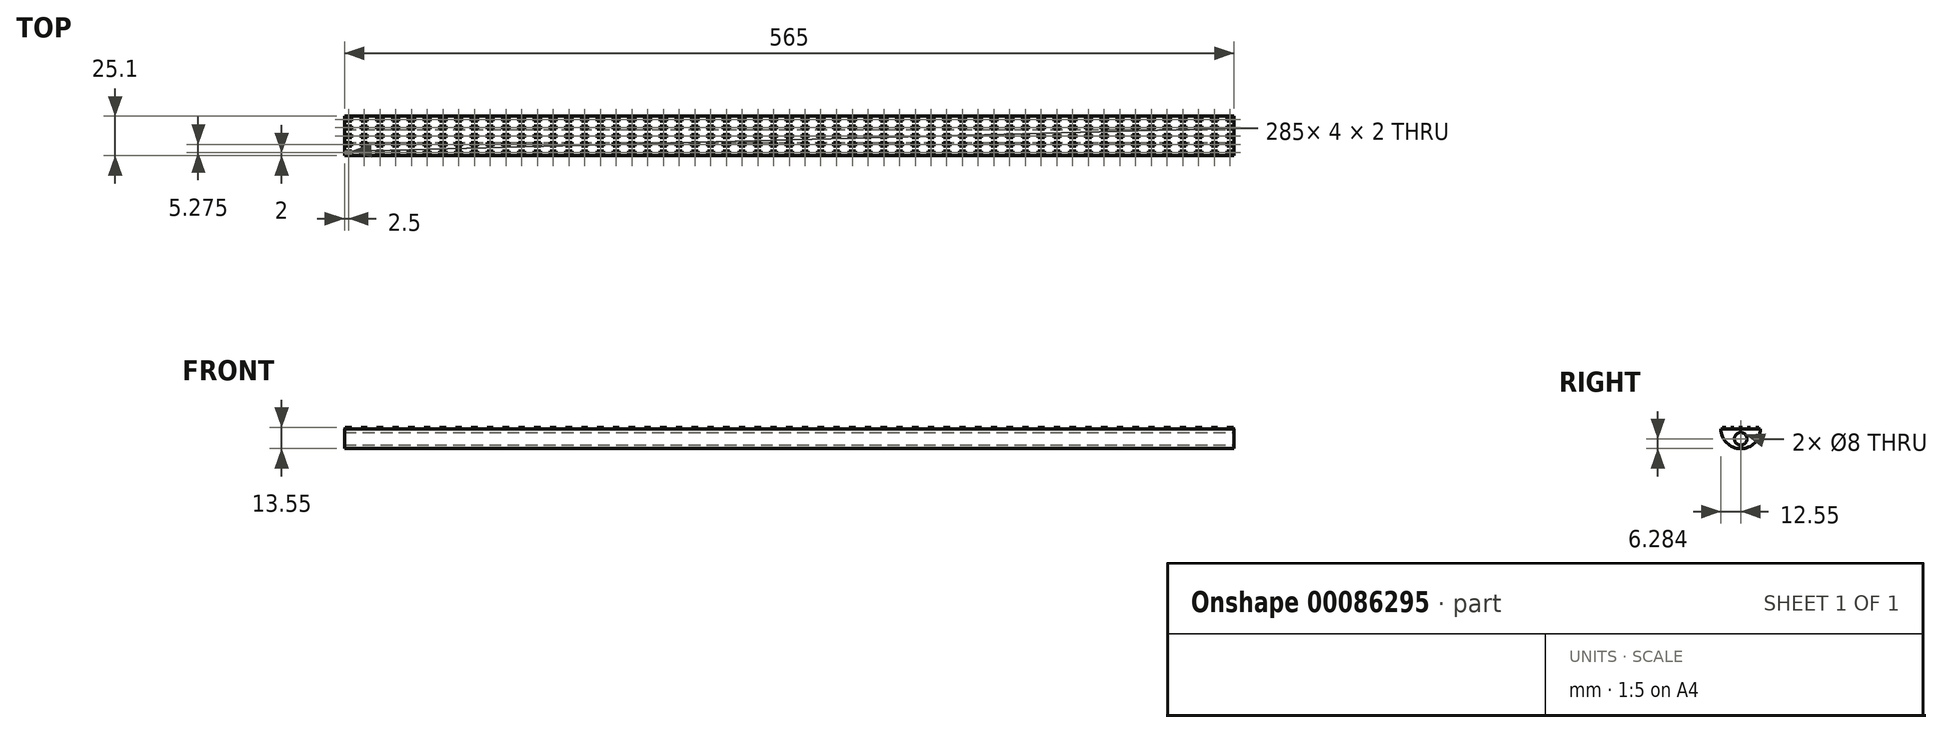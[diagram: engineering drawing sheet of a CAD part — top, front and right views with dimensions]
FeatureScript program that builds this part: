
annotation { "Feature Type Name" : "Feature", "Feature Type Description" : "" }
export const myFeature = defineFeature(function(context is Context, id is Id, definition is map)
    precondition{}
    {
        {
            var Q0;
            Q0=qCreatedBy(makeId("Right.planeOp"),FACE);
            var sketch = newSketch(context, id + "F0", { "sketchPlane" : qUnion([Q0])});
            skArc(sketch, "E0", {"start": v(-12.55, 0) * mm, "mid": v(0, -12.55) * mm, "end": v(12.55, 0) * mm});
            skLineSegment(sketch, "E1", {"start": v(-12.55, 0) * mm, "end": v(12.55, 0) * mm});
            skSolve(sketch);
        }
        {
            var Q0;
            Q0=qSketchRegion(id+"F0",true);
            extrude(context, id + "F1", {"entities" : qUnion([Q0]), "endBound" : BoundingType.SYMMETRIC, "depth" : 565 * mm});
        }
        {
            var Q0;
            Q0=makeQuery(id+"F1.opExtrude","SWEPT_FACE",FACE,{"disambiguationData":[OSD([sQuery(id+"F0.wireOp",EDGE,"E1")])]});
            var sketch = newSketch(context, id + "F2", { "sketchPlane" : qUnion([Q0])});
            skLineSegment(sketch, "E2.bottom", {"start": v(-282, 11.55) * mm, "end": v(-278, 11.55) * mm});
            skLineSegment(sketch, "E2.top", {"start": v(-282, 9.55) * mm, "end": v(-278, 9.55) * mm});
            skLineSegment(sketch, "E2.left", {"start": v(-282, 11.55) * mm, "end": v(-282, 9.55) * mm});
            skLineSegment(sketch, "E2.right", {"start": v(-278, 11.55) * mm, "end": v(-278, 9.55) * mm});
            skLineSegment(sketch, "E3.1.0.0", {"start": v(-282, 6.27) * mm, "end": v(-282, 4.27) * mm});
            skLineSegment(sketch, "E3.1.0.1", {"start": v(-282, 6.27) * mm, "end": v(-278, 6.27) * mm});
            skLineSegment(sketch, "E3.1.0.2", {"start": v(-278, 6.27) * mm, "end": v(-278, 4.27) * mm});
            skLineSegment(sketch, "E3.1.0.3", {"start": v(-282, 4.27) * mm, "end": v(-278, 4.27) * mm});
            skLineSegment(sketch, "E3.2.0.0", {"start": v(-282, 1) * mm, "end": v(-282, -1) * mm});
            skLineSegment(sketch, "E3.2.0.1", {"start": v(-282, 1) * mm, "end": v(-278, 1) * mm});
            skLineSegment(sketch, "E3.2.0.2", {"start": v(-278, 1) * mm, "end": v(-278, -1) * mm});
            skLineSegment(sketch, "E3.2.0.3", {"start": v(-282, -1) * mm, "end": v(-278, -1) * mm});
            skLineSegment(sketch, "E3.direction1", {"start": v(-278, 9.55) * mm, "end": v(-278, 4.27) * mm, "construction": true});
            skLineSegment(sketch, "E4.0.3.0", {"start": v(-282, -4.28) * mm, "end": v(-282, -6.28) * mm});
            skLineSegment(sketch, "E4.3.3.0", {"start": v(-282, -4.28) * mm, "end": v(-278, -4.28) * mm});
            skLineSegment(sketch, "E4.6.3.0", {"start": v(-278, -4.28) * mm, "end": v(-278, -6.28) * mm});
            skLineSegment(sketch, "E4.9.3.0", {"start": v(-282, -6.28) * mm, "end": v(-278, -6.28) * mm});
            skLineSegment(sketch, "E5.0.4.0", {"start": v(-282, -9.55) * mm, "end": v(-282, -11.55) * mm});
            skLineSegment(sketch, "E5.3.4.0", {"start": v(-282, -9.55) * mm, "end": v(-278, -9.55) * mm});
            skLineSegment(sketch, "E5.6.4.0", {"start": v(-278, -9.55) * mm, "end": v(-278, -11.55) * mm});
            skLineSegment(sketch, "E5.9.4.0", {"start": v(-282, -11.55) * mm, "end": v(-278, -11.55) * mm});
            skLineSegment(sketch, "E6.1.0.0", {"start": v(-272, -9.55) * mm, "end": v(-272, -11.55) * mm});
            skLineSegment(sketch, "E6.1.0.1", {"start": v(-268, -9.55) * mm, "end": v(-268, -11.55) * mm});
            skLineSegment(sketch, "E6.1.0.2", {"start": v(-272, -9.55) * mm, "end": v(-268, -9.55) * mm});
            skLineSegment(sketch, "E6.1.0.3", {"start": v(-268, 9.55) * mm, "end": v(-268, 4.27) * mm, "construction": true});
            skLineSegment(sketch, "E6.1.0.4", {"start": v(-272, -1) * mm, "end": v(-268, -1) * mm});
            skLineSegment(sketch, "E6.1.0.5", {"start": v(-272, -11.55) * mm, "end": v(-268, -11.55) * mm});
            skLineSegment(sketch, "E6.1.0.6", {"start": v(-268, 1) * mm, "end": v(-268, -1) * mm});
            skLineSegment(sketch, "E6.1.0.7", {"start": v(-272, 1) * mm, "end": v(-268, 1) * mm});
            skLineSegment(sketch, "E6.1.0.8", {"start": v(-272, 1) * mm, "end": v(-272, -1) * mm});
            skLineSegment(sketch, "E6.1.0.9", {"start": v(-272, 4.27) * mm, "end": v(-268, 4.27) * mm});
            skLineSegment(sketch, "E6.1.0.10", {"start": v(-268, 6.27) * mm, "end": v(-268, 4.27) * mm});
            skLineSegment(sketch, "E6.1.0.11", {"start": v(-272, 6.27) * mm, "end": v(-268, 6.27) * mm});
            skLineSegment(sketch, "E6.1.0.12", {"start": v(-272, 6.27) * mm, "end": v(-272, 4.27) * mm});
            skLineSegment(sketch, "E6.1.0.13", {"start": v(-268, 11.55) * mm, "end": v(-268, 9.55) * mm});
            skLineSegment(sketch, "E6.1.0.14", {"start": v(-272, 11.55) * mm, "end": v(-272, 9.55) * mm});
            skLineSegment(sketch, "E6.1.0.15", {"start": v(-272, 9.55) * mm, "end": v(-268, 9.55) * mm});
            skLineSegment(sketch, "E6.1.0.16", {"start": v(-272, -6.28) * mm, "end": v(-268, -6.28) * mm});
            skLineSegment(sketch, "E6.1.0.17", {"start": v(-272, 11.55) * mm, "end": v(-268, 11.55) * mm});
            skLineSegment(sketch, "E6.1.0.18", {"start": v(-268, -4.28) * mm, "end": v(-268, -6.28) * mm});
            skLineSegment(sketch, "E6.1.0.19", {"start": v(-272, -4.28) * mm, "end": v(-268, -4.28) * mm});
            skLineSegment(sketch, "E6.1.0.20", {"start": v(-272, -4.28) * mm, "end": v(-272, -6.28) * mm});
            skLineSegment(sketch, "E6.2.0.0", {"start": v(-262, -9.55) * mm, "end": v(-262, -11.55) * mm});
            skLineSegment(sketch, "E6.2.0.1", {"start": v(-258, -9.55) * mm, "end": v(-258, -11.55) * mm});
            skLineSegment(sketch, "E6.2.0.2", {"start": v(-262, -9.55) * mm, "end": v(-258, -9.55) * mm});
            skLineSegment(sketch, "E6.2.0.3", {"start": v(-258, 9.55) * mm, "end": v(-258, 4.27) * mm, "construction": true});
            skLineSegment(sketch, "E6.2.0.4", {"start": v(-262, -1) * mm, "end": v(-258, -1) * mm});
            skLineSegment(sketch, "E6.2.0.5", {"start": v(-262, -11.55) * mm, "end": v(-258, -11.55) * mm});
            skLineSegment(sketch, "E6.2.0.6", {"start": v(-258, 1) * mm, "end": v(-258, -1) * mm});
            skLineSegment(sketch, "E6.2.0.7", {"start": v(-262, 1) * mm, "end": v(-258, 1) * mm});
            skLineSegment(sketch, "E6.2.0.8", {"start": v(-262, 1) * mm, "end": v(-262, -1) * mm});
            skLineSegment(sketch, "E6.2.0.9", {"start": v(-262, 4.27) * mm, "end": v(-258, 4.27) * mm});
            skLineSegment(sketch, "E6.2.0.10", {"start": v(-258, 6.27) * mm, "end": v(-258, 4.27) * mm});
            skLineSegment(sketch, "E6.2.0.11", {"start": v(-262, 6.27) * mm, "end": v(-258, 6.27) * mm});
            skLineSegment(sketch, "E6.2.0.12", {"start": v(-262, 6.27) * mm, "end": v(-262, 4.27) * mm});
            skLineSegment(sketch, "E6.2.0.13", {"start": v(-258, 11.55) * mm, "end": v(-258, 9.55) * mm});
            skLineSegment(sketch, "E6.2.0.14", {"start": v(-262, 11.55) * mm, "end": v(-262, 9.55) * mm});
            skLineSegment(sketch, "E6.2.0.15", {"start": v(-262, 9.55) * mm, "end": v(-258, 9.55) * mm});
            skLineSegment(sketch, "E6.2.0.16", {"start": v(-262, -6.28) * mm, "end": v(-258, -6.28) * mm});
            skLineSegment(sketch, "E6.2.0.17", {"start": v(-262, 11.55) * mm, "end": v(-258, 11.55) * mm});
            skLineSegment(sketch, "E6.2.0.18", {"start": v(-258, -4.28) * mm, "end": v(-258, -6.28) * mm});
            skLineSegment(sketch, "E6.2.0.19", {"start": v(-262, -4.28) * mm, "end": v(-258, -4.28) * mm});
            skLineSegment(sketch, "E6.2.0.20", {"start": v(-262, -4.28) * mm, "end": v(-262, -6.28) * mm});
            skLineSegment(sketch, "E6.3.0.0", {"start": v(-252, -9.55) * mm, "end": v(-252, -11.55) * mm});
            skLineSegment(sketch, "E6.3.0.1", {"start": v(-248, -9.55) * mm, "end": v(-248, -11.55) * mm});
            skLineSegment(sketch, "E6.3.0.2", {"start": v(-252, -9.55) * mm, "end": v(-248, -9.55) * mm});
            skLineSegment(sketch, "E6.3.0.3", {"start": v(-248, 9.55) * mm, "end": v(-248, 4.27) * mm, "construction": true});
            skLineSegment(sketch, "E6.3.0.4", {"start": v(-252, -1) * mm, "end": v(-248, -1) * mm});
            skLineSegment(sketch, "E6.3.0.5", {"start": v(-252, -11.55) * mm, "end": v(-248, -11.55) * mm});
            skLineSegment(sketch, "E6.3.0.6", {"start": v(-248, 1) * mm, "end": v(-248, -1) * mm});
            skLineSegment(sketch, "E6.3.0.7", {"start": v(-252, 1) * mm, "end": v(-248, 1) * mm});
            skLineSegment(sketch, "E6.3.0.8", {"start": v(-252, 1) * mm, "end": v(-252, -1) * mm});
            skLineSegment(sketch, "E6.3.0.9", {"start": v(-252, 4.27) * mm, "end": v(-248, 4.27) * mm});
            skLineSegment(sketch, "E6.3.0.10", {"start": v(-248, 6.27) * mm, "end": v(-248, 4.27) * mm});
            skLineSegment(sketch, "E6.3.0.11", {"start": v(-252, 6.27) * mm, "end": v(-248, 6.27) * mm});
            skLineSegment(sketch, "E6.3.0.12", {"start": v(-252, 6.27) * mm, "end": v(-252, 4.27) * mm});
            skLineSegment(sketch, "E6.3.0.13", {"start": v(-248, 11.55) * mm, "end": v(-248, 9.55) * mm});
            skLineSegment(sketch, "E6.3.0.14", {"start": v(-252, 11.55) * mm, "end": v(-252, 9.55) * mm});
            skLineSegment(sketch, "E6.3.0.15", {"start": v(-252, 9.55) * mm, "end": v(-248, 9.55) * mm});
            skLineSegment(sketch, "E6.3.0.16", {"start": v(-252, -6.28) * mm, "end": v(-248, -6.28) * mm});
            skLineSegment(sketch, "E6.3.0.17", {"start": v(-252, 11.55) * mm, "end": v(-248, 11.55) * mm});
            skLineSegment(sketch, "E6.3.0.18", {"start": v(-248, -4.28) * mm, "end": v(-248, -6.28) * mm});
            skLineSegment(sketch, "E6.3.0.19", {"start": v(-252, -4.28) * mm, "end": v(-248, -4.28) * mm});
            skLineSegment(sketch, "E6.3.0.20", {"start": v(-252, -4.28) * mm, "end": v(-252, -6.28) * mm});
            skLineSegment(sketch, "E6.4.0.0", {"start": v(-242, -9.55) * mm, "end": v(-242, -11.55) * mm});
            skLineSegment(sketch, "E6.4.0.1", {"start": v(-238, -9.55) * mm, "end": v(-238, -11.55) * mm});
            skLineSegment(sketch, "E6.4.0.2", {"start": v(-242, -9.55) * mm, "end": v(-238, -9.55) * mm});
            skLineSegment(sketch, "E6.4.0.3", {"start": v(-238, 9.55) * mm, "end": v(-238, 4.27) * mm, "construction": true});
            skLineSegment(sketch, "E6.4.0.4", {"start": v(-242, -1) * mm, "end": v(-238, -1) * mm});
            skLineSegment(sketch, "E6.4.0.5", {"start": v(-242, -11.55) * mm, "end": v(-238, -11.55) * mm});
            skLineSegment(sketch, "E6.4.0.6", {"start": v(-238, 1) * mm, "end": v(-238, -1) * mm});
            skLineSegment(sketch, "E6.4.0.7", {"start": v(-242, 1) * mm, "end": v(-238, 1) * mm});
            skLineSegment(sketch, "E6.4.0.8", {"start": v(-242, 1) * mm, "end": v(-242, -1) * mm});
            skLineSegment(sketch, "E6.4.0.9", {"start": v(-242, 4.27) * mm, "end": v(-238, 4.27) * mm});
            skLineSegment(sketch, "E6.4.0.10", {"start": v(-238, 6.27) * mm, "end": v(-238, 4.27) * mm});
            skLineSegment(sketch, "E6.4.0.11", {"start": v(-242, 6.27) * mm, "end": v(-238, 6.27) * mm});
            skLineSegment(sketch, "E6.4.0.12", {"start": v(-242, 6.27) * mm, "end": v(-242, 4.27) * mm});
            skLineSegment(sketch, "E6.4.0.13", {"start": v(-238, 11.55) * mm, "end": v(-238, 9.55) * mm});
            skLineSegment(sketch, "E6.4.0.14", {"start": v(-242, 11.55) * mm, "end": v(-242, 9.55) * mm});
            skLineSegment(sketch, "E6.4.0.15", {"start": v(-242, 9.55) * mm, "end": v(-238, 9.55) * mm});
            skLineSegment(sketch, "E6.4.0.16", {"start": v(-242, -6.28) * mm, "end": v(-238, -6.28) * mm});
            skLineSegment(sketch, "E6.4.0.17", {"start": v(-242, 11.55) * mm, "end": v(-238, 11.55) * mm});
            skLineSegment(sketch, "E6.4.0.18", {"start": v(-238, -4.28) * mm, "end": v(-238, -6.28) * mm});
            skLineSegment(sketch, "E6.4.0.19", {"start": v(-242, -4.28) * mm, "end": v(-238, -4.28) * mm});
            skLineSegment(sketch, "E6.4.0.20", {"start": v(-242, -4.28) * mm, "end": v(-242, -6.28) * mm});
            skLineSegment(sketch, "E6.5.0.0", {"start": v(-232, -9.55) * mm, "end": v(-232, -11.55) * mm});
            skLineSegment(sketch, "E6.5.0.1", {"start": v(-228, -9.55) * mm, "end": v(-228, -11.55) * mm});
            skLineSegment(sketch, "E6.5.0.2", {"start": v(-232, -9.55) * mm, "end": v(-228, -9.55) * mm});
            skLineSegment(sketch, "E6.5.0.3", {"start": v(-228, 9.55) * mm, "end": v(-228, 4.27) * mm, "construction": true});
            skLineSegment(sketch, "E6.5.0.4", {"start": v(-232, -1) * mm, "end": v(-228, -1) * mm});
            skLineSegment(sketch, "E6.5.0.5", {"start": v(-232, -11.55) * mm, "end": v(-228, -11.55) * mm});
            skLineSegment(sketch, "E6.5.0.6", {"start": v(-228, 1) * mm, "end": v(-228, -1) * mm});
            skLineSegment(sketch, "E6.5.0.7", {"start": v(-232, 1) * mm, "end": v(-228, 1) * mm});
            skLineSegment(sketch, "E6.5.0.8", {"start": v(-232, 1) * mm, "end": v(-232, -1) * mm});
            skLineSegment(sketch, "E6.5.0.9", {"start": v(-232, 4.27) * mm, "end": v(-228, 4.27) * mm});
            skLineSegment(sketch, "E6.5.0.10", {"start": v(-228, 6.27) * mm, "end": v(-228, 4.27) * mm});
            skLineSegment(sketch, "E6.5.0.11", {"start": v(-232, 6.27) * mm, "end": v(-228, 6.27) * mm});
            skLineSegment(sketch, "E6.5.0.12", {"start": v(-232, 6.27) * mm, "end": v(-232, 4.27) * mm});
            skLineSegment(sketch, "E6.5.0.13", {"start": v(-228, 11.55) * mm, "end": v(-228, 9.55) * mm});
            skLineSegment(sketch, "E6.5.0.14", {"start": v(-232, 11.55) * mm, "end": v(-232, 9.55) * mm});
            skLineSegment(sketch, "E6.5.0.15", {"start": v(-232, 9.55) * mm, "end": v(-228, 9.55) * mm});
            skLineSegment(sketch, "E6.5.0.16", {"start": v(-232, -6.28) * mm, "end": v(-228, -6.28) * mm});
            skLineSegment(sketch, "E6.5.0.17", {"start": v(-232, 11.55) * mm, "end": v(-228, 11.55) * mm});
            skLineSegment(sketch, "E6.5.0.18", {"start": v(-228, -4.28) * mm, "end": v(-228, -6.28) * mm});
            skLineSegment(sketch, "E6.5.0.19", {"start": v(-232, -4.28) * mm, "end": v(-228, -4.28) * mm});
            skLineSegment(sketch, "E6.5.0.20", {"start": v(-232, -4.28) * mm, "end": v(-232, -6.28) * mm});
            skLineSegment(sketch, "E6.6.0.0", {"start": v(-222, -9.55) * mm, "end": v(-222, -11.55) * mm});
            skLineSegment(sketch, "E6.6.0.1", {"start": v(-218, -9.55) * mm, "end": v(-218, -11.55) * mm});
            skLineSegment(sketch, "E6.6.0.2", {"start": v(-222, -9.55) * mm, "end": v(-218, -9.55) * mm});
            skLineSegment(sketch, "E6.6.0.3", {"start": v(-218, 9.55) * mm, "end": v(-218, 4.27) * mm, "construction": true});
            skLineSegment(sketch, "E6.6.0.4", {"start": v(-222, -1) * mm, "end": v(-218, -1) * mm});
            skLineSegment(sketch, "E6.6.0.5", {"start": v(-222, -11.55) * mm, "end": v(-218, -11.55) * mm});
            skLineSegment(sketch, "E6.6.0.6", {"start": v(-218, 1) * mm, "end": v(-218, -1) * mm});
            skLineSegment(sketch, "E6.6.0.7", {"start": v(-222, 1) * mm, "end": v(-218, 1) * mm});
            skLineSegment(sketch, "E6.6.0.8", {"start": v(-222, 1) * mm, "end": v(-222, -1) * mm});
            skLineSegment(sketch, "E6.6.0.9", {"start": v(-222, 4.27) * mm, "end": v(-218, 4.27) * mm});
            skLineSegment(sketch, "E6.6.0.10", {"start": v(-218, 6.27) * mm, "end": v(-218, 4.27) * mm});
            skLineSegment(sketch, "E6.6.0.11", {"start": v(-222, 6.27) * mm, "end": v(-218, 6.27) * mm});
            skLineSegment(sketch, "E6.6.0.12", {"start": v(-222, 6.27) * mm, "end": v(-222, 4.27) * mm});
            skLineSegment(sketch, "E6.6.0.13", {"start": v(-218, 11.55) * mm, "end": v(-218, 9.55) * mm});
            skLineSegment(sketch, "E6.6.0.14", {"start": v(-222, 11.55) * mm, "end": v(-222, 9.55) * mm});
            skLineSegment(sketch, "E6.6.0.15", {"start": v(-222, 9.55) * mm, "end": v(-218, 9.55) * mm});
            skLineSegment(sketch, "E6.6.0.16", {"start": v(-222, -6.28) * mm, "end": v(-218, -6.28) * mm});
            skLineSegment(sketch, "E6.6.0.17", {"start": v(-222, 11.55) * mm, "end": v(-218, 11.55) * mm});
            skLineSegment(sketch, "E6.6.0.18", {"start": v(-218, -4.28) * mm, "end": v(-218, -6.28) * mm});
            skLineSegment(sketch, "E6.6.0.19", {"start": v(-222, -4.28) * mm, "end": v(-218, -4.28) * mm});
            skLineSegment(sketch, "E6.6.0.20", {"start": v(-222, -4.28) * mm, "end": v(-222, -6.28) * mm});
            skLineSegment(sketch, "E6.7.0.0", {"start": v(-212, -9.55) * mm, "end": v(-212, -11.55) * mm});
            skLineSegment(sketch, "E6.7.0.1", {"start": v(-208, -9.55) * mm, "end": v(-208, -11.55) * mm});
            skLineSegment(sketch, "E6.7.0.2", {"start": v(-212, -9.55) * mm, "end": v(-208, -9.55) * mm});
            skLineSegment(sketch, "E6.7.0.3", {"start": v(-208, 9.55) * mm, "end": v(-208, 4.27) * mm, "construction": true});
            skLineSegment(sketch, "E6.7.0.4", {"start": v(-212, -1) * mm, "end": v(-208, -1) * mm});
            skLineSegment(sketch, "E6.7.0.5", {"start": v(-212, -11.55) * mm, "end": v(-208, -11.55) * mm});
            skLineSegment(sketch, "E6.7.0.6", {"start": v(-208, 1) * mm, "end": v(-208, -1) * mm});
            skLineSegment(sketch, "E6.7.0.7", {"start": v(-212, 1) * mm, "end": v(-208, 1) * mm});
            skLineSegment(sketch, "E6.7.0.8", {"start": v(-212, 1) * mm, "end": v(-212, -1) * mm});
            skLineSegment(sketch, "E6.7.0.9", {"start": v(-212, 4.27) * mm, "end": v(-208, 4.27) * mm});
            skLineSegment(sketch, "E6.7.0.10", {"start": v(-208, 6.27) * mm, "end": v(-208, 4.27) * mm});
            skLineSegment(sketch, "E6.7.0.11", {"start": v(-212, 6.27) * mm, "end": v(-208, 6.27) * mm});
            skLineSegment(sketch, "E6.7.0.12", {"start": v(-212, 6.27) * mm, "end": v(-212, 4.27) * mm});
            skLineSegment(sketch, "E6.7.0.13", {"start": v(-208, 11.55) * mm, "end": v(-208, 9.55) * mm});
            skLineSegment(sketch, "E6.7.0.14", {"start": v(-212, 11.55) * mm, "end": v(-212, 9.55) * mm});
            skLineSegment(sketch, "E6.7.0.15", {"start": v(-212, 9.55) * mm, "end": v(-208, 9.55) * mm});
            skLineSegment(sketch, "E6.7.0.16", {"start": v(-212, -6.28) * mm, "end": v(-208, -6.28) * mm});
            skLineSegment(sketch, "E6.7.0.17", {"start": v(-212, 11.55) * mm, "end": v(-208, 11.55) * mm});
            skLineSegment(sketch, "E6.7.0.18", {"start": v(-208, -4.28) * mm, "end": v(-208, -6.28) * mm});
            skLineSegment(sketch, "E6.7.0.19", {"start": v(-212, -4.28) * mm, "end": v(-208, -4.28) * mm});
            skLineSegment(sketch, "E6.7.0.20", {"start": v(-212, -4.28) * mm, "end": v(-212, -6.28) * mm});
            skLineSegment(sketch, "E6.8.0.0", {"start": v(-202, -9.55) * mm, "end": v(-202, -11.55) * mm});
            skLineSegment(sketch, "E6.8.0.1", {"start": v(-198, -9.55) * mm, "end": v(-198, -11.55) * mm});
            skLineSegment(sketch, "E6.8.0.2", {"start": v(-202, -9.55) * mm, "end": v(-198, -9.55) * mm});
            skLineSegment(sketch, "E6.8.0.3", {"start": v(-198, 9.55) * mm, "end": v(-198, 4.27) * mm, "construction": true});
            skLineSegment(sketch, "E6.8.0.4", {"start": v(-202, -1) * mm, "end": v(-198, -1) * mm});
            skLineSegment(sketch, "E6.8.0.5", {"start": v(-202, -11.55) * mm, "end": v(-198, -11.55) * mm});
            skLineSegment(sketch, "E6.8.0.6", {"start": v(-198, 1) * mm, "end": v(-198, -1) * mm});
            skLineSegment(sketch, "E6.8.0.7", {"start": v(-202, 1) * mm, "end": v(-198, 1) * mm});
            skLineSegment(sketch, "E6.8.0.8", {"start": v(-202, 1) * mm, "end": v(-202, -1) * mm});
            skLineSegment(sketch, "E6.8.0.9", {"start": v(-202, 4.27) * mm, "end": v(-198, 4.27) * mm});
            skLineSegment(sketch, "E6.8.0.10", {"start": v(-198, 6.27) * mm, "end": v(-198, 4.27) * mm});
            skLineSegment(sketch, "E6.8.0.11", {"start": v(-202, 6.27) * mm, "end": v(-198, 6.27) * mm});
            skLineSegment(sketch, "E6.8.0.12", {"start": v(-202, 6.27) * mm, "end": v(-202, 4.27) * mm});
            skLineSegment(sketch, "E6.8.0.13", {"start": v(-198, 11.55) * mm, "end": v(-198, 9.55) * mm});
            skLineSegment(sketch, "E6.8.0.14", {"start": v(-202, 11.55) * mm, "end": v(-202, 9.55) * mm});
            skLineSegment(sketch, "E6.8.0.15", {"start": v(-202, 9.55) * mm, "end": v(-198, 9.55) * mm});
            skLineSegment(sketch, "E6.8.0.16", {"start": v(-202, -6.28) * mm, "end": v(-198, -6.28) * mm});
            skLineSegment(sketch, "E6.8.0.17", {"start": v(-202, 11.55) * mm, "end": v(-198, 11.55) * mm});
            skLineSegment(sketch, "E6.8.0.18", {"start": v(-198, -4.28) * mm, "end": v(-198, -6.28) * mm});
            skLineSegment(sketch, "E6.8.0.19", {"start": v(-202, -4.28) * mm, "end": v(-198, -4.28) * mm});
            skLineSegment(sketch, "E6.8.0.20", {"start": v(-202, -4.28) * mm, "end": v(-202, -6.28) * mm});
            skLineSegment(sketch, "E6.9.0.0", {"start": v(-192, -9.55) * mm, "end": v(-192, -11.55) * mm});
            skLineSegment(sketch, "E6.9.0.1", {"start": v(-188, -9.55) * mm, "end": v(-188, -11.55) * mm});
            skLineSegment(sketch, "E6.9.0.2", {"start": v(-192, -9.55) * mm, "end": v(-188, -9.55) * mm});
            skLineSegment(sketch, "E6.9.0.3", {"start": v(-188, 9.55) * mm, "end": v(-188, 4.27) * mm, "construction": true});
            skLineSegment(sketch, "E6.9.0.4", {"start": v(-192, -1) * mm, "end": v(-188, -1) * mm});
            skLineSegment(sketch, "E6.9.0.5", {"start": v(-192, -11.55) * mm, "end": v(-188, -11.55) * mm});
            skLineSegment(sketch, "E6.9.0.6", {"start": v(-188, 1) * mm, "end": v(-188, -1) * mm});
            skLineSegment(sketch, "E6.9.0.7", {"start": v(-192, 1) * mm, "end": v(-188, 1) * mm});
            skLineSegment(sketch, "E6.9.0.8", {"start": v(-192, 1) * mm, "end": v(-192, -1) * mm});
            skLineSegment(sketch, "E6.9.0.9", {"start": v(-192, 4.27) * mm, "end": v(-188, 4.27) * mm});
            skLineSegment(sketch, "E6.9.0.10", {"start": v(-188, 6.27) * mm, "end": v(-188, 4.27) * mm});
            skLineSegment(sketch, "E6.9.0.11", {"start": v(-192, 6.27) * mm, "end": v(-188, 6.27) * mm});
            skLineSegment(sketch, "E6.9.0.12", {"start": v(-192, 6.27) * mm, "end": v(-192, 4.27) * mm});
            skLineSegment(sketch, "E6.9.0.13", {"start": v(-188, 11.55) * mm, "end": v(-188, 9.55) * mm});
            skLineSegment(sketch, "E6.9.0.14", {"start": v(-192, 11.55) * mm, "end": v(-192, 9.55) * mm});
            skLineSegment(sketch, "E6.9.0.15", {"start": v(-192, 9.55) * mm, "end": v(-188, 9.55) * mm});
            skLineSegment(sketch, "E6.9.0.16", {"start": v(-192, -6.28) * mm, "end": v(-188, -6.28) * mm});
            skLineSegment(sketch, "E6.9.0.17", {"start": v(-192, 11.55) * mm, "end": v(-188, 11.55) * mm});
            skLineSegment(sketch, "E6.9.0.18", {"start": v(-188, -4.28) * mm, "end": v(-188, -6.28) * mm});
            skLineSegment(sketch, "E6.9.0.19", {"start": v(-192, -4.28) * mm, "end": v(-188, -4.28) * mm});
            skLineSegment(sketch, "E6.9.0.20", {"start": v(-192, -4.28) * mm, "end": v(-192, -6.28) * mm});
            skLineSegment(sketch, "E6.direction1", {"start": v(-282, -11.55) * mm, "end": v(-272, -11.55) * mm, "construction": true});
            skLineSegment(sketch, "E7.1.0.0", {"start": v(-172, -9.55) * mm, "end": v(-168, -9.55) * mm});
            skLineSegment(sketch, "E7.1.0.1", {"start": v(-168, -9.55) * mm, "end": v(-168, -11.55) * mm});
            skLineSegment(sketch, "E7.1.0.2", {"start": v(-102, 11.55) * mm, "end": v(-102, 9.55) * mm});
            skLineSegment(sketch, "E7.1.0.3", {"start": v(-112, -1) * mm, "end": v(-108, -1) * mm});
            skLineSegment(sketch, "E7.1.0.4", {"start": v(-132, 11.55) * mm, "end": v(-132, 9.55) * mm});
            skLineSegment(sketch, "E7.1.0.5", {"start": v(-102, 9.55) * mm, "end": v(-98, 9.55) * mm});
            skLineSegment(sketch, "E7.1.0.6", {"start": v(-162, 11.55) * mm, "end": v(-162, 9.55) * mm});
            skLineSegment(sketch, "E7.1.0.7", {"start": v(-132, 9.55) * mm, "end": v(-128, 9.55) * mm});
            skLineSegment(sketch, "E7.1.0.8", {"start": v(-102, -9.55) * mm, "end": v(-102, -11.55) * mm});
            skLineSegment(sketch, "E7.1.0.9", {"start": v(-162, 9.55) * mm, "end": v(-158, 9.55) * mm});
            skLineSegment(sketch, "E7.1.0.10", {"start": v(-108, 1) * mm, "end": v(-108, -1) * mm});
            skLineSegment(sketch, "E7.1.0.11", {"start": v(-92, 6.27) * mm, "end": v(-92, 4.27) * mm});
            skLineSegment(sketch, "E7.1.0.12", {"start": v(-102, 11.55) * mm, "end": v(-98, 11.55) * mm});
            skLineSegment(sketch, "E7.1.0.13", {"start": v(-98, -9.55) * mm, "end": v(-98, -11.55) * mm});
            skLineSegment(sketch, "E7.1.0.14", {"start": v(-172, -11.55) * mm, "end": v(-168, -11.55) * mm});
            skLineSegment(sketch, "E7.1.0.15", {"start": v(-112, 1) * mm, "end": v(-108, 1) * mm});
            skLineSegment(sketch, "E7.1.0.16", {"start": v(-132, 11.55) * mm, "end": v(-128, 11.55) * mm});
            skLineSegment(sketch, "E7.1.0.17", {"start": v(-128, -9.55) * mm, "end": v(-128, -11.55) * mm});
            skLineSegment(sketch, "E7.1.0.18", {"start": v(-102, -9.55) * mm, "end": v(-98, -9.55) * mm});
            skLineSegment(sketch, "E7.1.0.19", {"start": v(-162, 11.55) * mm, "end": v(-158, 11.55) * mm});
            skLineSegment(sketch, "E7.1.0.20", {"start": v(-132, -9.55) * mm, "end": v(-128, -9.55) * mm});
            skLineSegment(sketch, "E7.1.0.21", {"start": v(-132, -1) * mm, "end": v(-128, -1) * mm});
            skLineSegment(sketch, "E7.1.0.22", {"start": v(-102, -11.55) * mm, "end": v(-98, -11.55) * mm});
            skLineSegment(sketch, "E7.1.0.23", {"start": v(-162, -1) * mm, "end": v(-158, -1) * mm});
            skLineSegment(sketch, "E7.1.0.24", {"start": v(-132, -11.55) * mm, "end": v(-128, -11.55) * mm});
            skLineSegment(sketch, "E7.1.0.25", {"start": v(-122, -9.55) * mm, "end": v(-122, -11.55) * mm});
            skLineSegment(sketch, "E7.1.0.26", {"start": v(-88, -9.55) * mm, "end": v(-88, -11.55) * mm});
            skLineSegment(sketch, "E7.1.0.27", {"start": v(-128, 1) * mm, "end": v(-128, -1) * mm});
            skLineSegment(sketch, "E7.1.0.28", {"start": v(-152, -9.55) * mm, "end": v(-152, -11.55) * mm});
            skLineSegment(sketch, "E7.1.0.29", {"start": v(-118, -9.55) * mm, "end": v(-118, -11.55) * mm});
            skLineSegment(sketch, "E7.1.0.30", {"start": v(-92, -9.55) * mm, "end": v(-88, -9.55) * mm});
            skLineSegment(sketch, "E7.1.0.31", {"start": v(-132, 1) * mm, "end": v(-128, 1) * mm});
            skLineSegment(sketch, "E7.1.0.32", {"start": v(-148, -9.55) * mm, "end": v(-148, -11.55) * mm});
            skLineSegment(sketch, "E7.1.0.33", {"start": v(-122, -9.55) * mm, "end": v(-118, -9.55) * mm});
            skLineSegment(sketch, "E7.1.0.34", {"start": v(-152, -9.55) * mm, "end": v(-148, -9.55) * mm});
            skLineSegment(sketch, "E7.1.0.35", {"start": v(-112, 11.55) * mm, "end": v(-112, 9.55) * mm});
            skLineSegment(sketch, "E7.1.0.36", {"start": v(-172, 6.27) * mm, "end": v(-172, 4.27) * mm});
            skLineSegment(sketch, "E7.1.0.37", {"start": v(-112, 9.55) * mm, "end": v(-108, 9.55) * mm});
            skLineSegment(sketch, "E7.1.0.38", {"start": v(-92, -11.55) * mm, "end": v(-88, -11.55) * mm});
            skLineSegment(sketch, "E7.1.0.39", {"start": v(-162, 1) * mm, "end": v(-162, -1) * mm});
            skLineSegment(sketch, "E7.1.0.40", {"start": v(-122, -11.55) * mm, "end": v(-118, -11.55) * mm});
            skLineSegment(sketch, "E7.1.0.41", {"start": v(-182, 11.55) * mm, "end": v(-178, 11.55) * mm});
            skLineSegment(sketch, "E7.1.0.42", {"start": v(-182, 9.55) * mm, "end": v(-178, 9.55) * mm});
            skLineSegment(sketch, "E7.1.0.43", {"start": v(-182, 11.55) * mm, "end": v(-182, 9.55) * mm});
            skLineSegment(sketch, "E7.1.0.44", {"start": v(-182, 6.27) * mm, "end": v(-182, 4.27) * mm});
            skLineSegment(sketch, "E7.1.0.45", {"start": v(-182, 6.27) * mm, "end": v(-178, 6.27) * mm});
            skLineSegment(sketch, "E7.1.0.46", {"start": v(-182, 4.27) * mm, "end": v(-178, 4.27) * mm});
            skLineSegment(sketch, "E7.1.0.47", {"start": v(-152, -11.55) * mm, "end": v(-148, -11.55) * mm});
            skLineSegment(sketch, "E7.1.0.48", {"start": v(-112, 11.55) * mm, "end": v(-108, 11.55) * mm});
            skLineSegment(sketch, "E7.1.0.49", {"start": v(-162, 6.27) * mm, "end": v(-162, 4.27) * mm});
            skLineSegment(sketch, "E7.1.0.50", {"start": v(-172, 11.55) * mm, "end": v(-168, 11.55) * mm});
            skLineSegment(sketch, "E7.1.0.51", {"start": v(-128, 11.55) * mm, "end": v(-128, 9.55) * mm});
            skLineSegment(sketch, "E7.1.0.52", {"start": v(-138, -4.28) * mm, "end": v(-138, -6.28) * mm});
            skLineSegment(sketch, "E7.1.0.53", {"start": v(-142, -9.55) * mm, "end": v(-138, -9.55) * mm});
            skLineSegment(sketch, "E7.1.0.54", {"start": v(-152, 1) * mm, "end": v(-148, 1) * mm});
            skLineSegment(sketch, "E7.1.0.55", {"start": v(-112, -4.28) * mm, "end": v(-108, -4.28) * mm});
            skLineSegment(sketch, "E7.1.0.56", {"start": v(-92, 4.27) * mm, "end": v(-88, 4.27) * mm});
            skLineSegment(sketch, "E7.1.0.57", {"start": v(-138, 9.55) * mm, "end": v(-138, 4.27) * mm, "construction": true});
            skLineSegment(sketch, "E7.1.0.58", {"start": v(-152, 1) * mm, "end": v(-152, -1) * mm});
            skLineSegment(sketch, "E7.1.0.59", {"start": v(-158, 11.55) * mm, "end": v(-158, 9.55) * mm});
            skLineSegment(sketch, "E7.1.0.60", {"start": v(-168, -4.28) * mm, "end": v(-168, -6.28) * mm});
            skLineSegment(sketch, "E7.1.0.61", {"start": v(-122, 4.27) * mm, "end": v(-118, 4.27) * mm});
            skLineSegment(sketch, "E7.1.0.62", {"start": v(-142, -4.28) * mm, "end": v(-138, -4.28) * mm});
            skLineSegment(sketch, "E7.1.0.63", {"start": v(-88, 6.27) * mm, "end": v(-88, 4.27) * mm});
            skLineSegment(sketch, "E7.1.0.64", {"start": v(-112, -4.28) * mm, "end": v(-112, -6.28) * mm});
            skLineSegment(sketch, "E7.1.0.65", {"start": v(-168, 9.55) * mm, "end": v(-168, 4.27) * mm, "construction": true});
            skLineSegment(sketch, "E7.1.0.66", {"start": v(-142, -1) * mm, "end": v(-138, -1) * mm});
            skLineSegment(sketch, "E7.1.0.67", {"start": v(-152, 4.27) * mm, "end": v(-148, 4.27) * mm});
            skLineSegment(sketch, "E7.1.0.68", {"start": v(-172, -4.28) * mm, "end": v(-168, -4.28) * mm});
            skLineSegment(sketch, "E7.1.0.69", {"start": v(-112, -11.55) * mm, "end": v(-108, -11.55) * mm});
            skLineSegment(sketch, "E7.1.0.70", {"start": v(-118, 6.27) * mm, "end": v(-118, 4.27) * mm});
            skLineSegment(sketch, "E7.1.0.71", {"start": v(-92, 6.27) * mm, "end": v(-88, 6.27) * mm});
            skLineSegment(sketch, "E7.1.0.72", {"start": v(-102, -6.28) * mm, "end": v(-98, -6.28) * mm});
            skLineSegment(sketch, "E7.1.0.73", {"start": v(-142, -11.55) * mm, "end": v(-138, -11.55) * mm});
            skLineSegment(sketch, "E7.1.0.74", {"start": v(-148, 6.27) * mm, "end": v(-148, 4.27) * mm});
            skLineSegment(sketch, "E7.1.0.75", {"start": v(-122, 6.27) * mm, "end": v(-118, 6.27) * mm});
            skLineSegment(sketch, "E7.1.0.76", {"start": v(-132, -6.28) * mm, "end": v(-128, -6.28) * mm});
            skLineSegment(sketch, "E7.1.0.77", {"start": v(-132, -9.55) * mm, "end": v(-132, -11.55) * mm});
            skLineSegment(sketch, "E7.1.0.78", {"start": v(-138, 1) * mm, "end": v(-138, -1) * mm});
            skLineSegment(sketch, "E7.1.0.79", {"start": v(-152, 6.27) * mm, "end": v(-148, 6.27) * mm});
            skLineSegment(sketch, "E7.1.0.80", {"start": v(-162, -6.28) * mm, "end": v(-158, -6.28) * mm});
            skLineSegment(sketch, "E7.1.0.81", {"start": v(-162, -9.55) * mm, "end": v(-162, -11.55) * mm});
            skLineSegment(sketch, "E7.1.0.82", {"start": v(-122, 6.27) * mm, "end": v(-122, 4.27) * mm});
            skLineSegment(sketch, "E7.1.0.83", {"start": v(-88, 11.55) * mm, "end": v(-88, 9.55) * mm});
            skLineSegment(sketch, "E7.1.0.84", {"start": v(-98, -4.28) * mm, "end": v(-98, -6.28) * mm});
            skLineSegment(sketch, "E7.1.0.85", {"start": v(-142, 1) * mm, "end": v(-138, 1) * mm});
            skLineSegment(sketch, "E7.1.0.86", {"start": v(-152, 6.27) * mm, "end": v(-152, 4.27) * mm});
            skLineSegment(sketch, "E7.1.0.87", {"start": v(-158, -9.55) * mm, "end": v(-158, -11.55) * mm});
            skLineSegment(sketch, "E7.1.0.88", {"start": v(-112, 1) * mm, "end": v(-112, -1) * mm});
            skLineSegment(sketch, "E7.1.0.89", {"start": v(-118, 11.55) * mm, "end": v(-118, 9.55) * mm});
            skLineSegment(sketch, "E7.1.0.90", {"start": v(-128, -4.28) * mm, "end": v(-128, -6.28) * mm});
            skLineSegment(sketch, "E7.1.0.91", {"start": v(-92, 11.55) * mm, "end": v(-92, 9.55) * mm});
            skLineSegment(sketch, "E7.1.0.92", {"start": v(-102, -4.28) * mm, "end": v(-98, -4.28) * mm});
            skLineSegment(sketch, "E7.1.0.93", {"start": v(-142, 4.27) * mm, "end": v(-138, 4.27) * mm});
            skLineSegment(sketch, "E7.1.0.94", {"start": v(-152, 11.55) * mm, "end": v(-152, 9.55) * mm});
            skLineSegment(sketch, "E7.1.0.95", {"start": v(-162, -4.28) * mm, "end": v(-158, -4.28) * mm});
            skLineSegment(sketch, "E7.1.0.96", {"start": v(-122, 9.55) * mm, "end": v(-118, 9.55) * mm});
            skLineSegment(sketch, "E7.1.0.97", {"start": v(-92, -6.28) * mm, "end": v(-88, -6.28) * mm});
            skLineSegment(sketch, "E7.1.0.98", {"start": v(-92, -9.55) * mm, "end": v(-92, -11.55) * mm});
            skLineSegment(sketch, "E7.1.0.99", {"start": v(-148, 11.55) * mm, "end": v(-148, 9.55) * mm});
            skLineSegment(sketch, "E7.1.0.100", {"start": v(-162, -9.55) * mm, "end": v(-158, -9.55) * mm});
            skLineSegment(sketch, "E7.1.0.101", {"start": v(-112, 4.27) * mm, "end": v(-108, 4.27) * mm});
            skLineSegment(sketch, "E7.1.0.102", {"start": v(-122, 11.55) * mm, "end": v(-122, 9.55) * mm});
            skLineSegment(sketch, "E7.1.0.103", {"start": v(-132, -4.28) * mm, "end": v(-128, -4.28) * mm});
            skLineSegment(sketch, "E7.1.0.104", {"start": v(-92, 9.55) * mm, "end": v(-88, 9.55) * mm});
            skLineSegment(sketch, "E7.1.0.105", {"start": v(-102, -1) * mm, "end": v(-98, -1) * mm});
            skLineSegment(sketch, "E7.1.0.106", {"start": v(-172, 4.27) * mm, "end": v(-168, 4.27) * mm});
            skLineSegment(sketch, "E7.1.0.107", {"start": v(-138, 6.27) * mm, "end": v(-138, 4.27) * mm});
            skLineSegment(sketch, "E7.1.0.108", {"start": v(-152, 9.55) * mm, "end": v(-148, 9.55) * mm});
            skLineSegment(sketch, "E7.1.0.109", {"start": v(-162, -4.28) * mm, "end": v(-162, -6.28) * mm});
            skLineSegment(sketch, "E7.1.0.110", {"start": v(-98, 1) * mm, "end": v(-98, -1) * mm});
            skLineSegment(sketch, "E7.1.0.111", {"start": v(-112, 6.27) * mm, "end": v(-108, 6.27) * mm});
            skLineSegment(sketch, "E7.1.0.112", {"start": v(-122, -6.28) * mm, "end": v(-118, -6.28) * mm});
            skLineSegment(sketch, "E7.1.0.113", {"start": v(-92, 11.55) * mm, "end": v(-88, 11.55) * mm});
            skLineSegment(sketch, "E7.1.0.114", {"start": v(-162, -11.55) * mm, "end": v(-158, -11.55) * mm});
            skLineSegment(sketch, "E7.1.0.115", {"start": v(-168, 6.27) * mm, "end": v(-168, 4.27) * mm});
            skLineSegment(sketch, "E7.1.0.116", {"start": v(-142, 6.27) * mm, "end": v(-138, 6.27) * mm});
            skLineSegment(sketch, "E7.1.0.117", {"start": v(-152, -6.28) * mm, "end": v(-148, -6.28) * mm});
            skLineSegment(sketch, "E7.1.0.118", {"start": v(-102, 1) * mm, "end": v(-98, 1) * mm});
            skLineSegment(sketch, "E7.1.0.119", {"start": v(-112, 6.27) * mm, "end": v(-112, 4.27) * mm});
            skLineSegment(sketch, "E7.1.0.120", {"start": v(-122, 11.55) * mm, "end": v(-118, 11.55) * mm});
            skLineSegment(sketch, "E7.1.0.121", {"start": v(-88, -4.28) * mm, "end": v(-88, -6.28) * mm});
            skLineSegment(sketch, "E7.1.0.122", {"start": v(-158, 1) * mm, "end": v(-158, -1) * mm});
            skLineSegment(sketch, "E7.1.0.123", {"start": v(-172, 6.27) * mm, "end": v(-168, 6.27) * mm});
            skLineSegment(sketch, "E7.1.0.124", {"start": v(-182, -6.28) * mm, "end": v(-178, -6.28) * mm});
            skLineSegment(sketch, "E7.1.0.125", {"start": v(-142, 6.27) * mm, "end": v(-142, 4.27) * mm});
            skLineSegment(sketch, "E7.1.0.126", {"start": v(-152, 11.55) * mm, "end": v(-148, 11.55) * mm});
            skLineSegment(sketch, "E7.1.0.127", {"start": v(-102, 1) * mm, "end": v(-102, -1) * mm});
            skLineSegment(sketch, "E7.1.0.128", {"start": v(-108, 11.55) * mm, "end": v(-108, 9.55) * mm});
            skLineSegment(sketch, "E7.1.0.129", {"start": v(-118, -4.28) * mm, "end": v(-118, -6.28) * mm});
            skLineSegment(sketch, "E7.1.0.130", {"start": v(-92, -4.28) * mm, "end": v(-88, -4.28) * mm});
            skLineSegment(sketch, "E7.1.0.131", {"start": v(-88, 9.55) * mm, "end": v(-88, 4.27) * mm, "construction": true});
            skLineSegment(sketch, "E7.1.0.132", {"start": v(-132, 1) * mm, "end": v(-132, -1) * mm});
            skLineSegment(sketch, "E7.1.0.133", {"start": v(-138, 11.55) * mm, "end": v(-138, 9.55) * mm});
            skLineSegment(sketch, "E7.1.0.134", {"start": v(-148, -4.28) * mm, "end": v(-148, -6.28) * mm});
            skLineSegment(sketch, "E7.1.0.135", {"start": v(-122, -4.28) * mm, "end": v(-118, -4.28) * mm});
            skLineSegment(sketch, "E7.1.0.136", {"start": v(-118, 9.55) * mm, "end": v(-118, 4.27) * mm, "construction": true});
            skLineSegment(sketch, "E7.1.0.137", {"start": v(-92, -4.28) * mm, "end": v(-92, -6.28) * mm});
            skLineSegment(sketch, "E7.1.0.138", {"start": v(-162, 1) * mm, "end": v(-158, 1) * mm});
            skLineSegment(sketch, "E7.1.0.139", {"start": v(-182, -9.55) * mm, "end": v(-182, -11.55) * mm});
            skLineSegment(sketch, "E7.1.0.140", {"start": v(-122, -4.28) * mm, "end": v(-122, -6.28) * mm});
            skLineSegment(sketch, "E7.1.0.141", {"start": v(-182, -11.55) * mm, "end": v(-172, -11.55) * mm, "construction": true});
            skLineSegment(sketch, "E7.1.0.142", {"start": v(-168, 11.55) * mm, "end": v(-168, 9.55) * mm});
            skLineSegment(sketch, "E7.1.0.143", {"start": v(-182, -9.55) * mm, "end": v(-178, -9.55) * mm});
            skLineSegment(sketch, "E7.1.0.144", {"start": v(-142, 11.55) * mm, "end": v(-142, 9.55) * mm});
            skLineSegment(sketch, "E7.1.0.145", {"start": v(-152, -4.28) * mm, "end": v(-148, -4.28) * mm});
            skLineSegment(sketch, "E7.1.0.146", {"start": v(-148, 9.55) * mm, "end": v(-148, 4.27) * mm, "construction": true});
            skLineSegment(sketch, "E7.1.0.147", {"start": v(-162, 4.27) * mm, "end": v(-158, 4.27) * mm});
            skLineSegment(sketch, "E7.1.0.148", {"start": v(-172, 11.55) * mm, "end": v(-172, 9.55) * mm});
            skLineSegment(sketch, "E7.1.0.149", {"start": v(-178, -9.55) * mm, "end": v(-178, -11.55) * mm});
            skLineSegment(sketch, "E7.1.0.150", {"start": v(-142, 9.55) * mm, "end": v(-138, 9.55) * mm});
            skLineSegment(sketch, "E7.1.0.151", {"start": v(-152, -4.28) * mm, "end": v(-152, -6.28) * mm});
            skLineSegment(sketch, "E7.1.0.152", {"start": v(-152, -1) * mm, "end": v(-148, -1) * mm});
            skLineSegment(sketch, "E7.1.0.153", {"start": v(-112, -6.28) * mm, "end": v(-108, -6.28) * mm});
            skLineSegment(sketch, "E7.1.0.154", {"start": v(-112, -9.55) * mm, "end": v(-112, -11.55) * mm});
            skLineSegment(sketch, "E7.1.0.155", {"start": v(-182, -4.28) * mm, "end": v(-182, -6.28) * mm});
            skLineSegment(sketch, "E7.1.0.156", {"start": v(-182, -4.28) * mm, "end": v(-178, -4.28) * mm});
            skLineSegment(sketch, "E7.1.0.157", {"start": v(-178, -4.28) * mm, "end": v(-178, -6.28) * mm});
            skLineSegment(sketch, "E7.1.0.158", {"start": v(-178, 6.27) * mm, "end": v(-178, 4.27) * mm});
            skLineSegment(sketch, "E7.1.0.159", {"start": v(-182, 1) * mm, "end": v(-182, -1) * mm});
            skLineSegment(sketch, "E7.1.0.160", {"start": v(-182, 1) * mm, "end": v(-178, 1) * mm});
            skLineSegment(sketch, "E7.1.0.161", {"start": v(-172, 9.55) * mm, "end": v(-168, 9.55) * mm});
            skLineSegment(sketch, "E7.1.0.162", {"start": v(-182, -11.55) * mm, "end": v(-178, -11.55) * mm});
            skLineSegment(sketch, "E7.1.0.163", {"start": v(-182, -1) * mm, "end": v(-178, -1) * mm});
            skLineSegment(sketch, "E7.1.0.164", {"start": v(-142, -6.28) * mm, "end": v(-138, -6.28) * mm});
            skLineSegment(sketch, "E7.1.0.165", {"start": v(-142, -9.55) * mm, "end": v(-142, -11.55) * mm});
            skLineSegment(sketch, "E7.1.0.166", {"start": v(-108, -9.55) * mm, "end": v(-108, -11.55) * mm});
            skLineSegment(sketch, "E7.1.0.167", {"start": v(-162, 6.27) * mm, "end": v(-158, 6.27) * mm});
            skLineSegment(sketch, "E7.1.0.168", {"start": v(-172, -6.28) * mm, "end": v(-168, -6.28) * mm});
            skLineSegment(sketch, "E7.1.0.169", {"start": v(-172, -9.55) * mm, "end": v(-172, -11.55) * mm});
            skLineSegment(sketch, "E7.1.0.170", {"start": v(-142, 11.55) * mm, "end": v(-138, 11.55) * mm});
            skLineSegment(sketch, "E7.1.0.171", {"start": v(-138, -9.55) * mm, "end": v(-138, -11.55) * mm});
            skLineSegment(sketch, "E7.1.0.172", {"start": v(-148, 1) * mm, "end": v(-148, -1) * mm});
            skLineSegment(sketch, "E7.1.0.173", {"start": v(-112, -9.55) * mm, "end": v(-108, -9.55) * mm});
            skLineSegment(sketch, "E7.1.0.174", {"start": v(-108, 9.55) * mm, "end": v(-108, 4.27) * mm, "construction": true});
            skLineSegment(sketch, "E7.1.0.175", {"start": v(-122, 1) * mm, "end": v(-122, -1) * mm});
            skLineSegment(sketch, "E7.1.0.176", {"start": v(-142, -4.28) * mm, "end": v(-142, -6.28) * mm});
            skLineSegment(sketch, "E7.1.0.177", {"start": v(-172, -1) * mm, "end": v(-168, -1) * mm});
            skLineSegment(sketch, "E7.1.0.178", {"start": v(-172, -4.28) * mm, "end": v(-172, -6.28) * mm});
            skLineSegment(sketch, "E7.1.0.179", {"start": v(-168, 1) * mm, "end": v(-168, -1) * mm});
            skLineSegment(sketch, "E7.1.0.180", {"start": v(-98, 9.55) * mm, "end": v(-98, 4.27) * mm, "construction": true});
            skLineSegment(sketch, "E7.1.0.181", {"start": v(-158, 9.55) * mm, "end": v(-158, 4.27) * mm, "construction": true});
            skLineSegment(sketch, "E7.1.0.182", {"start": v(-172, 1) * mm, "end": v(-172, -1) * mm});
            skLineSegment(sketch, "E7.1.0.183", {"start": v(-108, 6.27) * mm, "end": v(-108, 4.27) * mm});
            skLineSegment(sketch, "E7.1.0.184", {"start": v(-132, -4.28) * mm, "end": v(-132, -6.28) * mm});
            skLineSegment(sketch, "E7.1.0.185", {"start": v(-172, 1) * mm, "end": v(-168, 1) * mm});
            skLineSegment(sketch, "E7.1.0.186", {"start": v(-142, 1) * mm, "end": v(-142, -1) * mm});
            skLineSegment(sketch, "E7.1.0.187", {"start": v(-158, -4.28) * mm, "end": v(-158, -6.28) * mm});
            skLineSegment(sketch, "E7.1.0.188", {"start": v(-128, 9.55) * mm, "end": v(-128, 4.27) * mm, "construction": true});
            skLineSegment(sketch, "E7.1.0.189", {"start": v(-102, -4.28) * mm, "end": v(-102, -6.28) * mm});
            skLineSegment(sketch, "E7.1.0.190", {"start": v(-102, 4.27) * mm, "end": v(-98, 4.27) * mm});
            skLineSegment(sketch, "E7.1.0.191", {"start": v(-92, -1) * mm, "end": v(-88, -1) * mm});
            skLineSegment(sketch, "E7.1.0.192", {"start": v(-98, 6.27) * mm, "end": v(-98, 4.27) * mm});
            skLineSegment(sketch, "E7.1.0.193", {"start": v(-122, -1) * mm, "end": v(-118, -1) * mm});
            skLineSegment(sketch, "E7.1.0.194", {"start": v(-132, 4.27) * mm, "end": v(-128, 4.27) * mm});
            skLineSegment(sketch, "E7.1.0.195", {"start": v(-88, 1) * mm, "end": v(-88, -1) * mm});
            skLineSegment(sketch, "E7.1.0.196", {"start": v(-128, 6.27) * mm, "end": v(-128, 4.27) * mm});
            skLineSegment(sketch, "E7.1.0.197", {"start": v(-102, 6.27) * mm, "end": v(-98, 6.27) * mm});
            skLineSegment(sketch, "E7.1.0.198", {"start": v(-178, 11.55) * mm, "end": v(-178, 9.55) * mm});
            skLineSegment(sketch, "E7.1.0.199", {"start": v(-178, 1) * mm, "end": v(-178, -1) * mm});
            skLineSegment(sketch, "E7.1.0.200", {"start": v(-158, 6.27) * mm, "end": v(-158, 4.27) * mm});
            skLineSegment(sketch, "E7.1.0.201", {"start": v(-132, 6.27) * mm, "end": v(-128, 6.27) * mm});
            skLineSegment(sketch, "E7.1.0.202", {"start": v(-178, 9.55) * mm, "end": v(-178, 4.27) * mm, "construction": true});
            skLineSegment(sketch, "E7.1.0.203", {"start": v(-102, 6.27) * mm, "end": v(-102, 4.27) * mm});
            skLineSegment(sketch, "E7.1.0.204", {"start": v(-118, 1) * mm, "end": v(-118, -1) * mm});
            skLineSegment(sketch, "E7.1.0.205", {"start": v(-92, 1) * mm, "end": v(-88, 1) * mm});
            skLineSegment(sketch, "E7.1.0.206", {"start": v(-132, 6.27) * mm, "end": v(-132, 4.27) * mm});
            skLineSegment(sketch, "E7.1.0.207", {"start": v(-98, 11.55) * mm, "end": v(-98, 9.55) * mm});
            skLineSegment(sketch, "E7.1.0.208", {"start": v(-108, -4.28) * mm, "end": v(-108, -6.28) * mm});
            skLineSegment(sketch, "E7.1.0.209", {"start": v(-122, 1) * mm, "end": v(-118, 1) * mm});
            skLineSegment(sketch, "E7.1.0.210", {"start": v(-92, 1) * mm, "end": v(-92, -1) * mm});
            skLineSegment(sketch, "E7.2.0.0", {"start": v(-72, -9.55) * mm, "end": v(-68, -9.55) * mm});
            skLineSegment(sketch, "E7.2.0.1", {"start": v(-68, -9.55) * mm, "end": v(-68, -11.55) * mm});
            skLineSegment(sketch, "E7.2.0.2", {"start": v(-2, 11.55) * mm, "end": v(-2, 9.55) * mm});
            skLineSegment(sketch, "E7.2.0.3", {"start": v(-12, -1) * mm, "end": v(-8, -1) * mm});
            skLineSegment(sketch, "E7.2.0.4", {"start": v(-32, 11.55) * mm, "end": v(-32, 9.55) * mm});
            skLineSegment(sketch, "E7.2.0.5", {"start": v(-2, 9.55) * mm, "end": v(2, 9.55) * mm});
            skLineSegment(sketch, "E7.2.0.6", {"start": v(-62, 11.55) * mm, "end": v(-62, 9.55) * mm});
            skLineSegment(sketch, "E7.2.0.7", {"start": v(-32, 9.55) * mm, "end": v(-28, 9.55) * mm});
            skLineSegment(sketch, "E7.2.0.8", {"start": v(-2, -9.55) * mm, "end": v(-2, -11.55) * mm});
            skLineSegment(sketch, "E7.2.0.9", {"start": v(-62, 9.55) * mm, "end": v(-58, 9.55) * mm});
            skLineSegment(sketch, "E7.2.0.10", {"start": v(-8, 1) * mm, "end": v(-8, -1) * mm});
            skLineSegment(sketch, "E7.2.0.11", {"start": v(8, 6.27) * mm, "end": v(8, 4.27) * mm});
            skLineSegment(sketch, "E7.2.0.12", {"start": v(-2, 11.55) * mm, "end": v(2, 11.55) * mm});
            skLineSegment(sketch, "E7.2.0.13", {"start": v(2, -9.55) * mm, "end": v(2, -11.55) * mm});
            skLineSegment(sketch, "E7.2.0.14", {"start": v(-72, -11.55) * mm, "end": v(-68, -11.55) * mm});
            skLineSegment(sketch, "E7.2.0.15", {"start": v(-12, 1) * mm, "end": v(-8, 1) * mm});
            skLineSegment(sketch, "E7.2.0.16", {"start": v(-32, 11.55) * mm, "end": v(-28, 11.55) * mm});
            skLineSegment(sketch, "E7.2.0.17", {"start": v(-28, -9.55) * mm, "end": v(-28, -11.55) * mm});
            skLineSegment(sketch, "E7.2.0.18", {"start": v(-2, -9.55) * mm, "end": v(2, -9.55) * mm});
            skLineSegment(sketch, "E7.2.0.19", {"start": v(-62, 11.55) * mm, "end": v(-58, 11.55) * mm});
            skLineSegment(sketch, "E7.2.0.20", {"start": v(-32, -9.55) * mm, "end": v(-28, -9.55) * mm});
            skLineSegment(sketch, "E7.2.0.21", {"start": v(-32, -1) * mm, "end": v(-28, -1) * mm});
            skLineSegment(sketch, "E7.2.0.22", {"start": v(-2, -11.55) * mm, "end": v(2, -11.55) * mm});
            skLineSegment(sketch, "E7.2.0.23", {"start": v(-62, -1) * mm, "end": v(-58, -1) * mm});
            skLineSegment(sketch, "E7.2.0.24", {"start": v(-32, -11.55) * mm, "end": v(-28, -11.55) * mm});
            skLineSegment(sketch, "E7.2.0.25", {"start": v(-22, -9.55) * mm, "end": v(-22, -11.55) * mm});
            skLineSegment(sketch, "E7.2.0.26", {"start": v(12, -9.55) * mm, "end": v(12, -11.55) * mm});
            skLineSegment(sketch, "E7.2.0.27", {"start": v(-28, 1) * mm, "end": v(-28, -1) * mm});
            skLineSegment(sketch, "E7.2.0.28", {"start": v(-52, -9.55) * mm, "end": v(-52, -11.55) * mm});
            skLineSegment(sketch, "E7.2.0.29", {"start": v(-18, -9.55) * mm, "end": v(-18, -11.55) * mm});
            skLineSegment(sketch, "E7.2.0.30", {"start": v(8, -9.55) * mm, "end": v(12, -9.55) * mm});
            skLineSegment(sketch, "E7.2.0.31", {"start": v(-32, 1) * mm, "end": v(-28, 1) * mm});
            skLineSegment(sketch, "E7.2.0.32", {"start": v(-48, -9.55) * mm, "end": v(-48, -11.55) * mm});
            skLineSegment(sketch, "E7.2.0.33", {"start": v(-22, -9.55) * mm, "end": v(-18, -9.55) * mm});
            skLineSegment(sketch, "E7.2.0.34", {"start": v(-52, -9.55) * mm, "end": v(-48, -9.55) * mm});
            skLineSegment(sketch, "E7.2.0.35", {"start": v(-12, 11.55) * mm, "end": v(-12, 9.55) * mm});
            skLineSegment(sketch, "E7.2.0.36", {"start": v(-72, 6.27) * mm, "end": v(-72, 4.27) * mm});
            skLineSegment(sketch, "E7.2.0.37", {"start": v(-12, 9.55) * mm, "end": v(-8, 9.55) * mm});
            skLineSegment(sketch, "E7.2.0.38", {"start": v(8, -11.55) * mm, "end": v(12, -11.55) * mm});
            skLineSegment(sketch, "E7.2.0.39", {"start": v(-62, 1) * mm, "end": v(-62, -1) * mm});
            skLineSegment(sketch, "E7.2.0.40", {"start": v(-22, -11.55) * mm, "end": v(-18, -11.55) * mm});
            skLineSegment(sketch, "E7.2.0.41", {"start": v(-82, 11.55) * mm, "end": v(-78, 11.55) * mm});
            skLineSegment(sketch, "E7.2.0.42", {"start": v(-82, 9.55) * mm, "end": v(-78, 9.55) * mm});
            skLineSegment(sketch, "E7.2.0.43", {"start": v(-82, 11.55) * mm, "end": v(-82, 9.55) * mm});
            skLineSegment(sketch, "E7.2.0.44", {"start": v(-82, 6.27) * mm, "end": v(-82, 4.27) * mm});
            skLineSegment(sketch, "E7.2.0.45", {"start": v(-82, 6.27) * mm, "end": v(-78, 6.27) * mm});
            skLineSegment(sketch, "E7.2.0.46", {"start": v(-82, 4.27) * mm, "end": v(-78, 4.27) * mm});
            skLineSegment(sketch, "E7.2.0.47", {"start": v(-52, -11.55) * mm, "end": v(-48, -11.55) * mm});
            skLineSegment(sketch, "E7.2.0.48", {"start": v(-12, 11.55) * mm, "end": v(-8, 11.55) * mm});
            skLineSegment(sketch, "E7.2.0.49", {"start": v(-62, 6.27) * mm, "end": v(-62, 4.27) * mm});
            skLineSegment(sketch, "E7.2.0.50", {"start": v(-72, 11.55) * mm, "end": v(-68, 11.55) * mm});
            skLineSegment(sketch, "E7.2.0.51", {"start": v(-28, 11.55) * mm, "end": v(-28, 9.55) * mm});
            skLineSegment(sketch, "E7.2.0.52", {"start": v(-38, -4.28) * mm, "end": v(-38, -6.28) * mm});
            skLineSegment(sketch, "E7.2.0.53", {"start": v(-42, -9.55) * mm, "end": v(-38, -9.55) * mm});
            skLineSegment(sketch, "E7.2.0.54", {"start": v(-52, 1) * mm, "end": v(-48, 1) * mm});
            skLineSegment(sketch, "E7.2.0.55", {"start": v(-12, -4.28) * mm, "end": v(-8, -4.28) * mm});
            skLineSegment(sketch, "E7.2.0.56", {"start": v(8, 4.27) * mm, "end": v(12, 4.27) * mm});
            skLineSegment(sketch, "E7.2.0.57", {"start": v(-38, 9.55) * mm, "end": v(-38, 4.27) * mm, "construction": true});
            skLineSegment(sketch, "E7.2.0.58", {"start": v(-52, 1) * mm, "end": v(-52, -1) * mm});
            skLineSegment(sketch, "E7.2.0.59", {"start": v(-58, 11.55) * mm, "end": v(-58, 9.55) * mm});
            skLineSegment(sketch, "E7.2.0.60", {"start": v(-68, -4.28) * mm, "end": v(-68, -6.28) * mm});
            skLineSegment(sketch, "E7.2.0.61", {"start": v(-22, 4.27) * mm, "end": v(-18, 4.27) * mm});
            skLineSegment(sketch, "E7.2.0.62", {"start": v(-42, -4.28) * mm, "end": v(-38, -4.28) * mm});
            skLineSegment(sketch, "E7.2.0.63", {"start": v(12, 6.27) * mm, "end": v(12, 4.27) * mm});
            skLineSegment(sketch, "E7.2.0.64", {"start": v(-12, -4.28) * mm, "end": v(-12, -6.28) * mm});
            skLineSegment(sketch, "E7.2.0.65", {"start": v(-68, 9.55) * mm, "end": v(-68, 4.27) * mm, "construction": true});
            skLineSegment(sketch, "E7.2.0.66", {"start": v(-42, -1) * mm, "end": v(-38, -1) * mm});
            skLineSegment(sketch, "E7.2.0.67", {"start": v(-52, 4.27) * mm, "end": v(-48, 4.27) * mm});
            skLineSegment(sketch, "E7.2.0.68", {"start": v(-72, -4.28) * mm, "end": v(-68, -4.28) * mm});
            skLineSegment(sketch, "E7.2.0.69", {"start": v(-12, -11.55) * mm, "end": v(-8, -11.55) * mm});
            skLineSegment(sketch, "E7.2.0.70", {"start": v(-18, 6.27) * mm, "end": v(-18, 4.27) * mm});
            skLineSegment(sketch, "E7.2.0.71", {"start": v(8, 6.27) * mm, "end": v(12, 6.27) * mm});
            skLineSegment(sketch, "E7.2.0.72", {"start": v(-2, -6.28) * mm, "end": v(2, -6.28) * mm});
            skLineSegment(sketch, "E7.2.0.73", {"start": v(-42, -11.55) * mm, "end": v(-38, -11.55) * mm});
            skLineSegment(sketch, "E7.2.0.74", {"start": v(-48, 6.27) * mm, "end": v(-48, 4.27) * mm});
            skLineSegment(sketch, "E7.2.0.75", {"start": v(-22, 6.27) * mm, "end": v(-18, 6.27) * mm});
            skLineSegment(sketch, "E7.2.0.76", {"start": v(-32, -6.28) * mm, "end": v(-28, -6.28) * mm});
            skLineSegment(sketch, "E7.2.0.77", {"start": v(-32, -9.55) * mm, "end": v(-32, -11.55) * mm});
            skLineSegment(sketch, "E7.2.0.78", {"start": v(-38, 1) * mm, "end": v(-38, -1) * mm});
            skLineSegment(sketch, "E7.2.0.79", {"start": v(-52, 6.27) * mm, "end": v(-48, 6.27) * mm});
            skLineSegment(sketch, "E7.2.0.80", {"start": v(-62, -6.28) * mm, "end": v(-58, -6.28) * mm});
            skLineSegment(sketch, "E7.2.0.81", {"start": v(-62, -9.55) * mm, "end": v(-62, -11.55) * mm});
            skLineSegment(sketch, "E7.2.0.82", {"start": v(-22, 6.27) * mm, "end": v(-22, 4.27) * mm});
            skLineSegment(sketch, "E7.2.0.83", {"start": v(12, 11.55) * mm, "end": v(12, 9.55) * mm});
            skLineSegment(sketch, "E7.2.0.84", {"start": v(2, -4.28) * mm, "end": v(2, -6.28) * mm});
            skLineSegment(sketch, "E7.2.0.85", {"start": v(-42, 1) * mm, "end": v(-38, 1) * mm});
            skLineSegment(sketch, "E7.2.0.86", {"start": v(-52, 6.27) * mm, "end": v(-52, 4.27) * mm});
            skLineSegment(sketch, "E7.2.0.87", {"start": v(-58, -9.55) * mm, "end": v(-58, -11.55) * mm});
            skLineSegment(sketch, "E7.2.0.88", {"start": v(-12, 1) * mm, "end": v(-12, -1) * mm});
            skLineSegment(sketch, "E7.2.0.89", {"start": v(-18, 11.55) * mm, "end": v(-18, 9.55) * mm});
            skLineSegment(sketch, "E7.2.0.90", {"start": v(-28, -4.28) * mm, "end": v(-28, -6.28) * mm});
            skLineSegment(sketch, "E7.2.0.91", {"start": v(8, 11.55) * mm, "end": v(8, 9.55) * mm});
            skLineSegment(sketch, "E7.2.0.92", {"start": v(-2, -4.28) * mm, "end": v(2, -4.28) * mm});
            skLineSegment(sketch, "E7.2.0.93", {"start": v(-42, 4.27) * mm, "end": v(-38, 4.27) * mm});
            skLineSegment(sketch, "E7.2.0.94", {"start": v(-52, 11.55) * mm, "end": v(-52, 9.55) * mm});
            skLineSegment(sketch, "E7.2.0.95", {"start": v(-62, -4.28) * mm, "end": v(-58, -4.28) * mm});
            skLineSegment(sketch, "E7.2.0.96", {"start": v(-22, 9.55) * mm, "end": v(-18, 9.55) * mm});
            skLineSegment(sketch, "E7.2.0.97", {"start": v(8, -6.28) * mm, "end": v(12, -6.28) * mm});
            skLineSegment(sketch, "E7.2.0.98", {"start": v(8, -9.55) * mm, "end": v(8, -11.55) * mm});
            skLineSegment(sketch, "E7.2.0.99", {"start": v(-48, 11.55) * mm, "end": v(-48, 9.55) * mm});
            skLineSegment(sketch, "E7.2.0.100", {"start": v(-62, -9.55) * mm, "end": v(-58, -9.55) * mm});
            skLineSegment(sketch, "E7.2.0.101", {"start": v(-12, 4.27) * mm, "end": v(-8, 4.27) * mm});
            skLineSegment(sketch, "E7.2.0.102", {"start": v(-22, 11.55) * mm, "end": v(-22, 9.55) * mm});
            skLineSegment(sketch, "E7.2.0.103", {"start": v(-32, -4.28) * mm, "end": v(-28, -4.28) * mm});
            skLineSegment(sketch, "E7.2.0.104", {"start": v(8, 9.55) * mm, "end": v(12, 9.55) * mm});
            skLineSegment(sketch, "E7.2.0.105", {"start": v(-2, -1) * mm, "end": v(2, -1) * mm});
            skLineSegment(sketch, "E7.2.0.106", {"start": v(-72, 4.27) * mm, "end": v(-68, 4.27) * mm});
            skLineSegment(sketch, "E7.2.0.107", {"start": v(-38, 6.27) * mm, "end": v(-38, 4.27) * mm});
            skLineSegment(sketch, "E7.2.0.108", {"start": v(-52, 9.55) * mm, "end": v(-48, 9.55) * mm});
            skLineSegment(sketch, "E7.2.0.109", {"start": v(-62, -4.28) * mm, "end": v(-62, -6.28) * mm});
            skLineSegment(sketch, "E7.2.0.110", {"start": v(2, 1) * mm, "end": v(2, -1) * mm});
            skLineSegment(sketch, "E7.2.0.111", {"start": v(-12, 6.27) * mm, "end": v(-8, 6.27) * mm});
            skLineSegment(sketch, "E7.2.0.112", {"start": v(-22, -6.28) * mm, "end": v(-18, -6.28) * mm});
            skLineSegment(sketch, "E7.2.0.113", {"start": v(8, 11.55) * mm, "end": v(12, 11.55) * mm});
            skLineSegment(sketch, "E7.2.0.114", {"start": v(-62, -11.55) * mm, "end": v(-58, -11.55) * mm});
            skLineSegment(sketch, "E7.2.0.115", {"start": v(-68, 6.27) * mm, "end": v(-68, 4.27) * mm});
            skLineSegment(sketch, "E7.2.0.116", {"start": v(-42, 6.27) * mm, "end": v(-38, 6.27) * mm});
            skLineSegment(sketch, "E7.2.0.117", {"start": v(-52, -6.28) * mm, "end": v(-48, -6.28) * mm});
            skLineSegment(sketch, "E7.2.0.118", {"start": v(-2, 1) * mm, "end": v(2, 1) * mm});
            skLineSegment(sketch, "E7.2.0.119", {"start": v(-12, 6.27) * mm, "end": v(-12, 4.27) * mm});
            skLineSegment(sketch, "E7.2.0.120", {"start": v(-22, 11.55) * mm, "end": v(-18, 11.55) * mm});
            skLineSegment(sketch, "E7.2.0.121", {"start": v(12, -4.28) * mm, "end": v(12, -6.28) * mm});
            skLineSegment(sketch, "E7.2.0.122", {"start": v(-58, 1) * mm, "end": v(-58, -1) * mm});
            skLineSegment(sketch, "E7.2.0.123", {"start": v(-72, 6.27) * mm, "end": v(-68, 6.27) * mm});
            skLineSegment(sketch, "E7.2.0.124", {"start": v(-82, -6.28) * mm, "end": v(-78, -6.28) * mm});
            skLineSegment(sketch, "E7.2.0.125", {"start": v(-42, 6.27) * mm, "end": v(-42, 4.27) * mm});
            skLineSegment(sketch, "E7.2.0.126", {"start": v(-52, 11.55) * mm, "end": v(-48, 11.55) * mm});
            skLineSegment(sketch, "E7.2.0.127", {"start": v(-2, 1) * mm, "end": v(-2, -1) * mm});
            skLineSegment(sketch, "E7.2.0.128", {"start": v(-8, 11.55) * mm, "end": v(-8, 9.55) * mm});
            skLineSegment(sketch, "E7.2.0.129", {"start": v(-18, -4.28) * mm, "end": v(-18, -6.28) * mm});
            skLineSegment(sketch, "E7.2.0.130", {"start": v(8, -4.28) * mm, "end": v(12, -4.28) * mm});
            skLineSegment(sketch, "E7.2.0.131", {"start": v(12, 9.55) * mm, "end": v(12, 4.27) * mm, "construction": true});
            skLineSegment(sketch, "E7.2.0.132", {"start": v(-32, 1) * mm, "end": v(-32, -1) * mm});
            skLineSegment(sketch, "E7.2.0.133", {"start": v(-38, 11.55) * mm, "end": v(-38, 9.55) * mm});
            skLineSegment(sketch, "E7.2.0.134", {"start": v(-48, -4.28) * mm, "end": v(-48, -6.28) * mm});
            skLineSegment(sketch, "E7.2.0.135", {"start": v(-22, -4.28) * mm, "end": v(-18, -4.28) * mm});
            skLineSegment(sketch, "E7.2.0.136", {"start": v(-18, 9.55) * mm, "end": v(-18, 4.27) * mm, "construction": true});
            skLineSegment(sketch, "E7.2.0.137", {"start": v(8, -4.28) * mm, "end": v(8, -6.28) * mm});
            skLineSegment(sketch, "E7.2.0.138", {"start": v(-62, 1) * mm, "end": v(-58, 1) * mm});
            skLineSegment(sketch, "E7.2.0.139", {"start": v(-82, -9.55) * mm, "end": v(-82, -11.55) * mm});
            skLineSegment(sketch, "E7.2.0.140", {"start": v(-22, -4.28) * mm, "end": v(-22, -6.28) * mm});
            skLineSegment(sketch, "E7.2.0.141", {"start": v(-82, -11.55) * mm, "end": v(-72, -11.55) * mm, "construction": true});
            skLineSegment(sketch, "E7.2.0.142", {"start": v(-68, 11.55) * mm, "end": v(-68, 9.55) * mm});
            skLineSegment(sketch, "E7.2.0.143", {"start": v(-82, -9.55) * mm, "end": v(-78, -9.55) * mm});
            skLineSegment(sketch, "E7.2.0.144", {"start": v(-42, 11.55) * mm, "end": v(-42, 9.55) * mm});
            skLineSegment(sketch, "E7.2.0.145", {"start": v(-52, -4.28) * mm, "end": v(-48, -4.28) * mm});
            skLineSegment(sketch, "E7.2.0.146", {"start": v(-48, 9.55) * mm, "end": v(-48, 4.27) * mm, "construction": true});
            skLineSegment(sketch, "E7.2.0.147", {"start": v(-62, 4.27) * mm, "end": v(-58, 4.27) * mm});
            skLineSegment(sketch, "E7.2.0.148", {"start": v(-72, 11.55) * mm, "end": v(-72, 9.55) * mm});
            skLineSegment(sketch, "E7.2.0.149", {"start": v(-78, -9.55) * mm, "end": v(-78, -11.55) * mm});
            skLineSegment(sketch, "E7.2.0.150", {"start": v(-42, 9.55) * mm, "end": v(-38, 9.55) * mm});
            skLineSegment(sketch, "E7.2.0.151", {"start": v(-52, -4.28) * mm, "end": v(-52, -6.28) * mm});
            skLineSegment(sketch, "E7.2.0.152", {"start": v(-52, -1) * mm, "end": v(-48, -1) * mm});
            skLineSegment(sketch, "E7.2.0.153", {"start": v(-12, -6.28) * mm, "end": v(-8, -6.28) * mm});
            skLineSegment(sketch, "E7.2.0.154", {"start": v(-12, -9.55) * mm, "end": v(-12, -11.55) * mm});
            skLineSegment(sketch, "E7.2.0.155", {"start": v(-82, -4.28) * mm, "end": v(-82, -6.28) * mm});
            skLineSegment(sketch, "E7.2.0.156", {"start": v(-82, -4.28) * mm, "end": v(-78, -4.28) * mm});
            skLineSegment(sketch, "E7.2.0.157", {"start": v(-78, -4.28) * mm, "end": v(-78, -6.28) * mm});
            skLineSegment(sketch, "E7.2.0.158", {"start": v(-78, 6.27) * mm, "end": v(-78, 4.27) * mm});
            skLineSegment(sketch, "E7.2.0.159", {"start": v(-82, 1) * mm, "end": v(-82, -1) * mm});
            skLineSegment(sketch, "E7.2.0.160", {"start": v(-82, 1) * mm, "end": v(-78, 1) * mm});
            skLineSegment(sketch, "E7.2.0.161", {"start": v(-72, 9.55) * mm, "end": v(-68, 9.55) * mm});
            skLineSegment(sketch, "E7.2.0.162", {"start": v(-82, -11.55) * mm, "end": v(-78, -11.55) * mm});
            skLineSegment(sketch, "E7.2.0.163", {"start": v(-82, -1) * mm, "end": v(-78, -1) * mm});
            skLineSegment(sketch, "E7.2.0.164", {"start": v(-42, -6.28) * mm, "end": v(-38, -6.28) * mm});
            skLineSegment(sketch, "E7.2.0.165", {"start": v(-42, -9.55) * mm, "end": v(-42, -11.55) * mm});
            skLineSegment(sketch, "E7.2.0.166", {"start": v(-8, -9.55) * mm, "end": v(-8, -11.55) * mm});
            skLineSegment(sketch, "E7.2.0.167", {"start": v(-62, 6.27) * mm, "end": v(-58, 6.27) * mm});
            skLineSegment(sketch, "E7.2.0.168", {"start": v(-72, -6.28) * mm, "end": v(-68, -6.28) * mm});
            skLineSegment(sketch, "E7.2.0.169", {"start": v(-72, -9.55) * mm, "end": v(-72, -11.55) * mm});
            skLineSegment(sketch, "E7.2.0.170", {"start": v(-42, 11.55) * mm, "end": v(-38, 11.55) * mm});
            skLineSegment(sketch, "E7.2.0.171", {"start": v(-38, -9.55) * mm, "end": v(-38, -11.55) * mm});
            skLineSegment(sketch, "E7.2.0.172", {"start": v(-48, 1) * mm, "end": v(-48, -1) * mm});
            skLineSegment(sketch, "E7.2.0.173", {"start": v(-12, -9.55) * mm, "end": v(-8, -9.55) * mm});
            skLineSegment(sketch, "E7.2.0.174", {"start": v(-8, 9.55) * mm, "end": v(-8, 4.27) * mm, "construction": true});
            skLineSegment(sketch, "E7.2.0.175", {"start": v(-22, 1) * mm, "end": v(-22, -1) * mm});
            skLineSegment(sketch, "E7.2.0.176", {"start": v(-42, -4.28) * mm, "end": v(-42, -6.28) * mm});
            skLineSegment(sketch, "E7.2.0.177", {"start": v(-72, -1) * mm, "end": v(-68, -1) * mm});
            skLineSegment(sketch, "E7.2.0.178", {"start": v(-72, -4.28) * mm, "end": v(-72, -6.28) * mm});
            skLineSegment(sketch, "E7.2.0.179", {"start": v(-68, 1) * mm, "end": v(-68, -1) * mm});
            skLineSegment(sketch, "E7.2.0.180", {"start": v(2, 9.55) * mm, "end": v(2, 4.27) * mm, "construction": true});
            skLineSegment(sketch, "E7.2.0.181", {"start": v(-58, 9.55) * mm, "end": v(-58, 4.27) * mm, "construction": true});
            skLineSegment(sketch, "E7.2.0.182", {"start": v(-72, 1) * mm, "end": v(-72, -1) * mm});
            skLineSegment(sketch, "E7.2.0.183", {"start": v(-8, 6.27) * mm, "end": v(-8, 4.27) * mm});
            skLineSegment(sketch, "E7.2.0.184", {"start": v(-32, -4.28) * mm, "end": v(-32, -6.28) * mm});
            skLineSegment(sketch, "E7.2.0.185", {"start": v(-72, 1) * mm, "end": v(-68, 1) * mm});
            skLineSegment(sketch, "E7.2.0.186", {"start": v(-42, 1) * mm, "end": v(-42, -1) * mm});
            skLineSegment(sketch, "E7.2.0.187", {"start": v(-58, -4.28) * mm, "end": v(-58, -6.28) * mm});
            skLineSegment(sketch, "E7.2.0.188", {"start": v(-28, 9.55) * mm, "end": v(-28, 4.27) * mm, "construction": true});
            skLineSegment(sketch, "E7.2.0.189", {"start": v(-2, -4.28) * mm, "end": v(-2, -6.28) * mm});
            skLineSegment(sketch, "E7.2.0.190", {"start": v(-2, 4.27) * mm, "end": v(2, 4.27) * mm});
            skLineSegment(sketch, "E7.2.0.191", {"start": v(8, -1) * mm, "end": v(12, -1) * mm});
            skLineSegment(sketch, "E7.2.0.192", {"start": v(2, 6.27) * mm, "end": v(2, 4.27) * mm});
            skLineSegment(sketch, "E7.2.0.193", {"start": v(-22, -1) * mm, "end": v(-18, -1) * mm});
            skLineSegment(sketch, "E7.2.0.194", {"start": v(-32, 4.27) * mm, "end": v(-28, 4.27) * mm});
            skLineSegment(sketch, "E7.2.0.195", {"start": v(12, 1) * mm, "end": v(12, -1) * mm});
            skLineSegment(sketch, "E7.2.0.196", {"start": v(-28, 6.27) * mm, "end": v(-28, 4.27) * mm});
            skLineSegment(sketch, "E7.2.0.197", {"start": v(-2, 6.27) * mm, "end": v(2, 6.27) * mm});
            skLineSegment(sketch, "E7.2.0.198", {"start": v(-78, 11.55) * mm, "end": v(-78, 9.55) * mm});
            skLineSegment(sketch, "E7.2.0.199", {"start": v(-78, 1) * mm, "end": v(-78, -1) * mm});
            skLineSegment(sketch, "E7.2.0.200", {"start": v(-58, 6.27) * mm, "end": v(-58, 4.27) * mm});
            skLineSegment(sketch, "E7.2.0.201", {"start": v(-32, 6.27) * mm, "end": v(-28, 6.27) * mm});
            skLineSegment(sketch, "E7.2.0.202", {"start": v(-78, 9.55) * mm, "end": v(-78, 4.27) * mm, "construction": true});
            skLineSegment(sketch, "E7.2.0.203", {"start": v(-2, 6.27) * mm, "end": v(-2, 4.27) * mm});
            skLineSegment(sketch, "E7.2.0.204", {"start": v(-18, 1) * mm, "end": v(-18, -1) * mm});
            skLineSegment(sketch, "E7.2.0.205", {"start": v(8, 1) * mm, "end": v(12, 1) * mm});
            skLineSegment(sketch, "E7.2.0.206", {"start": v(-32, 6.27) * mm, "end": v(-32, 4.27) * mm});
            skLineSegment(sketch, "E7.2.0.207", {"start": v(2, 11.55) * mm, "end": v(2, 9.55) * mm});
            skLineSegment(sketch, "E7.2.0.208", {"start": v(-8, -4.28) * mm, "end": v(-8, -6.28) * mm});
            skLineSegment(sketch, "E7.2.0.209", {"start": v(-22, 1) * mm, "end": v(-18, 1) * mm});
            skLineSegment(sketch, "E7.2.0.210", {"start": v(8, 1) * mm, "end": v(8, -1) * mm});
            skLineSegment(sketch, "E7.3.0.0", {"start": v(28, -9.55) * mm, "end": v(32, -9.55) * mm});
            skLineSegment(sketch, "E7.3.0.1", {"start": v(32, -9.55) * mm, "end": v(32, -11.55) * mm});
            skLineSegment(sketch, "E7.3.0.2", {"start": v(98, 11.55) * mm, "end": v(98, 9.55) * mm});
            skLineSegment(sketch, "E7.3.0.3", {"start": v(88, -1) * mm, "end": v(92, -1) * mm});
            skLineSegment(sketch, "E7.3.0.4", {"start": v(68, 11.55) * mm, "end": v(68, 9.55) * mm});
            skLineSegment(sketch, "E7.3.0.5", {"start": v(98, 9.55) * mm, "end": v(102, 9.55) * mm});
            skLineSegment(sketch, "E7.3.0.6", {"start": v(38, 11.55) * mm, "end": v(38, 9.55) * mm});
            skLineSegment(sketch, "E7.3.0.7", {"start": v(68, 9.55) * mm, "end": v(72, 9.55) * mm});
            skLineSegment(sketch, "E7.3.0.8", {"start": v(98, -9.55) * mm, "end": v(98, -11.55) * mm});
            skLineSegment(sketch, "E7.3.0.9", {"start": v(38, 9.55) * mm, "end": v(42, 9.55) * mm});
            skLineSegment(sketch, "E7.3.0.10", {"start": v(92, 1) * mm, "end": v(92, -1) * mm});
            skLineSegment(sketch, "E7.3.0.11", {"start": v(108, 6.27) * mm, "end": v(108, 4.27) * mm});
            skLineSegment(sketch, "E7.3.0.12", {"start": v(98, 11.55) * mm, "end": v(102, 11.55) * mm});
            skLineSegment(sketch, "E7.3.0.13", {"start": v(102, -9.55) * mm, "end": v(102, -11.55) * mm});
            skLineSegment(sketch, "E7.3.0.14", {"start": v(28, -11.55) * mm, "end": v(32, -11.55) * mm});
            skLineSegment(sketch, "E7.3.0.15", {"start": v(88, 1) * mm, "end": v(92, 1) * mm});
            skLineSegment(sketch, "E7.3.0.16", {"start": v(68, 11.55) * mm, "end": v(72, 11.55) * mm});
            skLineSegment(sketch, "E7.3.0.17", {"start": v(72, -9.55) * mm, "end": v(72, -11.55) * mm});
            skLineSegment(sketch, "E7.3.0.18", {"start": v(98, -9.55) * mm, "end": v(102, -9.55) * mm});
            skLineSegment(sketch, "E7.3.0.19", {"start": v(38, 11.55) * mm, "end": v(42, 11.55) * mm});
            skLineSegment(sketch, "E7.3.0.20", {"start": v(68, -9.55) * mm, "end": v(72, -9.55) * mm});
            skLineSegment(sketch, "E7.3.0.21", {"start": v(68, -1) * mm, "end": v(72, -1) * mm});
            skLineSegment(sketch, "E7.3.0.22", {"start": v(98, -11.55) * mm, "end": v(102, -11.55) * mm});
            skLineSegment(sketch, "E7.3.0.23", {"start": v(38, -1) * mm, "end": v(42, -1) * mm});
            skLineSegment(sketch, "E7.3.0.24", {"start": v(68, -11.55) * mm, "end": v(72, -11.55) * mm});
            skLineSegment(sketch, "E7.3.0.25", {"start": v(78, -9.55) * mm, "end": v(78, -11.55) * mm});
            skLineSegment(sketch, "E7.3.0.26", {"start": v(112, -9.55) * mm, "end": v(112, -11.55) * mm});
            skLineSegment(sketch, "E7.3.0.27", {"start": v(72, 1) * mm, "end": v(72, -1) * mm});
            skLineSegment(sketch, "E7.3.0.28", {"start": v(48, -9.55) * mm, "end": v(48, -11.55) * mm});
            skLineSegment(sketch, "E7.3.0.29", {"start": v(82, -9.55) * mm, "end": v(82, -11.55) * mm});
            skLineSegment(sketch, "E7.3.0.30", {"start": v(108, -9.55) * mm, "end": v(112, -9.55) * mm});
            skLineSegment(sketch, "E7.3.0.31", {"start": v(68, 1) * mm, "end": v(72, 1) * mm});
            skLineSegment(sketch, "E7.3.0.32", {"start": v(52, -9.55) * mm, "end": v(52, -11.55) * mm});
            skLineSegment(sketch, "E7.3.0.33", {"start": v(78, -9.55) * mm, "end": v(82, -9.55) * mm});
            skLineSegment(sketch, "E7.3.0.34", {"start": v(48, -9.55) * mm, "end": v(52, -9.55) * mm});
            skLineSegment(sketch, "E7.3.0.35", {"start": v(88, 11.55) * mm, "end": v(88, 9.55) * mm});
            skLineSegment(sketch, "E7.3.0.36", {"start": v(28, 6.27) * mm, "end": v(28, 4.27) * mm});
            skLineSegment(sketch, "E7.3.0.37", {"start": v(88, 9.55) * mm, "end": v(92, 9.55) * mm});
            skLineSegment(sketch, "E7.3.0.38", {"start": v(108, -11.55) * mm, "end": v(112, -11.55) * mm});
            skLineSegment(sketch, "E7.3.0.39", {"start": v(38, 1) * mm, "end": v(38, -1) * mm});
            skLineSegment(sketch, "E7.3.0.40", {"start": v(78, -11.55) * mm, "end": v(82, -11.55) * mm});
            skLineSegment(sketch, "E7.3.0.41", {"start": v(18, 11.55) * mm, "end": v(22, 11.55) * mm});
            skLineSegment(sketch, "E7.3.0.42", {"start": v(18, 9.55) * mm, "end": v(22, 9.55) * mm});
            skLineSegment(sketch, "E7.3.0.43", {"start": v(18, 11.55) * mm, "end": v(18, 9.55) * mm});
            skLineSegment(sketch, "E7.3.0.44", {"start": v(18, 6.27) * mm, "end": v(18, 4.27) * mm});
            skLineSegment(sketch, "E7.3.0.45", {"start": v(18, 6.27) * mm, "end": v(22, 6.27) * mm});
            skLineSegment(sketch, "E7.3.0.46", {"start": v(18, 4.27) * mm, "end": v(22, 4.27) * mm});
            skLineSegment(sketch, "E7.3.0.47", {"start": v(48, -11.55) * mm, "end": v(52, -11.55) * mm});
            skLineSegment(sketch, "E7.3.0.48", {"start": v(88, 11.55) * mm, "end": v(92, 11.55) * mm});
            skLineSegment(sketch, "E7.3.0.49", {"start": v(38, 6.27) * mm, "end": v(38, 4.27) * mm});
            skLineSegment(sketch, "E7.3.0.50", {"start": v(28, 11.55) * mm, "end": v(32, 11.55) * mm});
            skLineSegment(sketch, "E7.3.0.51", {"start": v(72, 11.55) * mm, "end": v(72, 9.55) * mm});
            skLineSegment(sketch, "E7.3.0.52", {"start": v(62, -4.28) * mm, "end": v(62, -6.28) * mm});
            skLineSegment(sketch, "E7.3.0.53", {"start": v(58, -9.55) * mm, "end": v(62, -9.55) * mm});
            skLineSegment(sketch, "E7.3.0.54", {"start": v(48, 1) * mm, "end": v(52, 1) * mm});
            skLineSegment(sketch, "E7.3.0.55", {"start": v(88, -4.28) * mm, "end": v(92, -4.28) * mm});
            skLineSegment(sketch, "E7.3.0.56", {"start": v(108, 4.27) * mm, "end": v(112, 4.27) * mm});
            skLineSegment(sketch, "E7.3.0.57", {"start": v(62, 9.55) * mm, "end": v(62, 4.27) * mm, "construction": true});
            skLineSegment(sketch, "E7.3.0.58", {"start": v(48, 1) * mm, "end": v(48, -1) * mm});
            skLineSegment(sketch, "E7.3.0.59", {"start": v(42, 11.55) * mm, "end": v(42, 9.55) * mm});
            skLineSegment(sketch, "E7.3.0.60", {"start": v(32, -4.28) * mm, "end": v(32, -6.28) * mm});
            skLineSegment(sketch, "E7.3.0.61", {"start": v(78, 4.27) * mm, "end": v(82, 4.27) * mm});
            skLineSegment(sketch, "E7.3.0.62", {"start": v(58, -4.28) * mm, "end": v(62, -4.28) * mm});
            skLineSegment(sketch, "E7.3.0.63", {"start": v(112, 6.27) * mm, "end": v(112, 4.27) * mm});
            skLineSegment(sketch, "E7.3.0.64", {"start": v(88, -4.28) * mm, "end": v(88, -6.28) * mm});
            skLineSegment(sketch, "E7.3.0.65", {"start": v(32, 9.55) * mm, "end": v(32, 4.27) * mm, "construction": true});
            skLineSegment(sketch, "E7.3.0.66", {"start": v(58, -1) * mm, "end": v(62, -1) * mm});
            skLineSegment(sketch, "E7.3.0.67", {"start": v(48, 4.27) * mm, "end": v(52, 4.27) * mm});
            skLineSegment(sketch, "E7.3.0.68", {"start": v(28, -4.28) * mm, "end": v(32, -4.28) * mm});
            skLineSegment(sketch, "E7.3.0.69", {"start": v(88, -11.55) * mm, "end": v(92, -11.55) * mm});
            skLineSegment(sketch, "E7.3.0.70", {"start": v(82, 6.27) * mm, "end": v(82, 4.27) * mm});
            skLineSegment(sketch, "E7.3.0.71", {"start": v(108, 6.27) * mm, "end": v(112, 6.27) * mm});
            skLineSegment(sketch, "E7.3.0.72", {"start": v(98, -6.28) * mm, "end": v(102, -6.28) * mm});
            skLineSegment(sketch, "E7.3.0.73", {"start": v(58, -11.55) * mm, "end": v(62, -11.55) * mm});
            skLineSegment(sketch, "E7.3.0.74", {"start": v(52, 6.27) * mm, "end": v(52, 4.27) * mm});
            skLineSegment(sketch, "E7.3.0.75", {"start": v(78, 6.27) * mm, "end": v(82, 6.27) * mm});
            skLineSegment(sketch, "E7.3.0.76", {"start": v(68, -6.28) * mm, "end": v(72, -6.28) * mm});
            skLineSegment(sketch, "E7.3.0.77", {"start": v(68, -9.55) * mm, "end": v(68, -11.55) * mm});
            skLineSegment(sketch, "E7.3.0.78", {"start": v(62, 1) * mm, "end": v(62, -1) * mm});
            skLineSegment(sketch, "E7.3.0.79", {"start": v(48, 6.27) * mm, "end": v(52, 6.27) * mm});
            skLineSegment(sketch, "E7.3.0.80", {"start": v(38, -6.28) * mm, "end": v(42, -6.28) * mm});
            skLineSegment(sketch, "E7.3.0.81", {"start": v(38, -9.55) * mm, "end": v(38, -11.55) * mm});
            skLineSegment(sketch, "E7.3.0.82", {"start": v(78, 6.27) * mm, "end": v(78, 4.27) * mm});
            skLineSegment(sketch, "E7.3.0.83", {"start": v(112, 11.55) * mm, "end": v(112, 9.55) * mm});
            skLineSegment(sketch, "E7.3.0.84", {"start": v(102, -4.28) * mm, "end": v(102, -6.28) * mm});
            skLineSegment(sketch, "E7.3.0.85", {"start": v(58, 1) * mm, "end": v(62, 1) * mm});
            skLineSegment(sketch, "E7.3.0.86", {"start": v(48, 6.27) * mm, "end": v(48, 4.27) * mm});
            skLineSegment(sketch, "E7.3.0.87", {"start": v(42, -9.55) * mm, "end": v(42, -11.55) * mm});
            skLineSegment(sketch, "E7.3.0.88", {"start": v(88, 1) * mm, "end": v(88, -1) * mm});
            skLineSegment(sketch, "E7.3.0.89", {"start": v(82, 11.55) * mm, "end": v(82, 9.55) * mm});
            skLineSegment(sketch, "E7.3.0.90", {"start": v(72, -4.28) * mm, "end": v(72, -6.28) * mm});
            skLineSegment(sketch, "E7.3.0.91", {"start": v(108, 11.55) * mm, "end": v(108, 9.55) * mm});
            skLineSegment(sketch, "E7.3.0.92", {"start": v(98, -4.28) * mm, "end": v(102, -4.28) * mm});
            skLineSegment(sketch, "E7.3.0.93", {"start": v(58, 4.27) * mm, "end": v(62, 4.27) * mm});
            skLineSegment(sketch, "E7.3.0.94", {"start": v(48, 11.55) * mm, "end": v(48, 9.55) * mm});
            skLineSegment(sketch, "E7.3.0.95", {"start": v(38, -4.28) * mm, "end": v(42, -4.28) * mm});
            skLineSegment(sketch, "E7.3.0.96", {"start": v(78, 9.55) * mm, "end": v(82, 9.55) * mm});
            skLineSegment(sketch, "E7.3.0.97", {"start": v(108, -6.28) * mm, "end": v(112, -6.28) * mm});
            skLineSegment(sketch, "E7.3.0.98", {"start": v(108, -9.55) * mm, "end": v(108, -11.55) * mm});
            skLineSegment(sketch, "E7.3.0.99", {"start": v(52, 11.55) * mm, "end": v(52, 9.55) * mm});
            skLineSegment(sketch, "E7.3.0.100", {"start": v(38, -9.55) * mm, "end": v(42, -9.55) * mm});
            skLineSegment(sketch, "E7.3.0.101", {"start": v(88, 4.27) * mm, "end": v(92, 4.27) * mm});
            skLineSegment(sketch, "E7.3.0.102", {"start": v(78, 11.55) * mm, "end": v(78, 9.55) * mm});
            skLineSegment(sketch, "E7.3.0.103", {"start": v(68, -4.28) * mm, "end": v(72, -4.28) * mm});
            skLineSegment(sketch, "E7.3.0.104", {"start": v(108, 9.55) * mm, "end": v(112, 9.55) * mm});
            skLineSegment(sketch, "E7.3.0.105", {"start": v(98, -1) * mm, "end": v(102, -1) * mm});
            skLineSegment(sketch, "E7.3.0.106", {"start": v(28, 4.27) * mm, "end": v(32, 4.27) * mm});
            skLineSegment(sketch, "E7.3.0.107", {"start": v(62, 6.27) * mm, "end": v(62, 4.27) * mm});
            skLineSegment(sketch, "E7.3.0.108", {"start": v(48, 9.55) * mm, "end": v(52, 9.55) * mm});
            skLineSegment(sketch, "E7.3.0.109", {"start": v(38, -4.28) * mm, "end": v(38, -6.28) * mm});
            skLineSegment(sketch, "E7.3.0.110", {"start": v(102, 1) * mm, "end": v(102, -1) * mm});
            skLineSegment(sketch, "E7.3.0.111", {"start": v(88, 6.27) * mm, "end": v(92, 6.27) * mm});
            skLineSegment(sketch, "E7.3.0.112", {"start": v(78, -6.28) * mm, "end": v(82, -6.28) * mm});
            skLineSegment(sketch, "E7.3.0.113", {"start": v(108, 11.55) * mm, "end": v(112, 11.55) * mm});
            skLineSegment(sketch, "E7.3.0.114", {"start": v(38, -11.55) * mm, "end": v(42, -11.55) * mm});
            skLineSegment(sketch, "E7.3.0.115", {"start": v(32, 6.27) * mm, "end": v(32, 4.27) * mm});
            skLineSegment(sketch, "E7.3.0.116", {"start": v(58, 6.27) * mm, "end": v(62, 6.27) * mm});
            skLineSegment(sketch, "E7.3.0.117", {"start": v(48, -6.28) * mm, "end": v(52, -6.28) * mm});
            skLineSegment(sketch, "E7.3.0.118", {"start": v(98, 1) * mm, "end": v(102, 1) * mm});
            skLineSegment(sketch, "E7.3.0.119", {"start": v(88, 6.27) * mm, "end": v(88, 4.27) * mm});
            skLineSegment(sketch, "E7.3.0.120", {"start": v(78, 11.55) * mm, "end": v(82, 11.55) * mm});
            skLineSegment(sketch, "E7.3.0.121", {"start": v(112, -4.28) * mm, "end": v(112, -6.28) * mm});
            skLineSegment(sketch, "E7.3.0.122", {"start": v(42, 1) * mm, "end": v(42, -1) * mm});
            skLineSegment(sketch, "E7.3.0.123", {"start": v(28, 6.27) * mm, "end": v(32, 6.27) * mm});
            skLineSegment(sketch, "E7.3.0.124", {"start": v(18, -6.28) * mm, "end": v(22, -6.28) * mm});
            skLineSegment(sketch, "E7.3.0.125", {"start": v(58, 6.27) * mm, "end": v(58, 4.27) * mm});
            skLineSegment(sketch, "E7.3.0.126", {"start": v(48, 11.55) * mm, "end": v(52, 11.55) * mm});
            skLineSegment(sketch, "E7.3.0.127", {"start": v(98, 1) * mm, "end": v(98, -1) * mm});
            skLineSegment(sketch, "E7.3.0.128", {"start": v(92, 11.55) * mm, "end": v(92, 9.55) * mm});
            skLineSegment(sketch, "E7.3.0.129", {"start": v(82, -4.28) * mm, "end": v(82, -6.28) * mm});
            skLineSegment(sketch, "E7.3.0.130", {"start": v(108, -4.28) * mm, "end": v(112, -4.28) * mm});
            skLineSegment(sketch, "E7.3.0.131", {"start": v(112, 9.55) * mm, "end": v(112, 4.27) * mm, "construction": true});
            skLineSegment(sketch, "E7.3.0.132", {"start": v(68, 1) * mm, "end": v(68, -1) * mm});
            skLineSegment(sketch, "E7.3.0.133", {"start": v(62, 11.55) * mm, "end": v(62, 9.55) * mm});
            skLineSegment(sketch, "E7.3.0.134", {"start": v(52, -4.28) * mm, "end": v(52, -6.28) * mm});
            skLineSegment(sketch, "E7.3.0.135", {"start": v(78, -4.28) * mm, "end": v(82, -4.28) * mm});
            skLineSegment(sketch, "E7.3.0.136", {"start": v(82, 9.55) * mm, "end": v(82, 4.27) * mm, "construction": true});
            skLineSegment(sketch, "E7.3.0.137", {"start": v(108, -4.28) * mm, "end": v(108, -6.28) * mm});
            skLineSegment(sketch, "E7.3.0.138", {"start": v(38, 1) * mm, "end": v(42, 1) * mm});
            skLineSegment(sketch, "E7.3.0.139", {"start": v(18, -9.55) * mm, "end": v(18, -11.55) * mm});
            skLineSegment(sketch, "E7.3.0.140", {"start": v(78, -4.28) * mm, "end": v(78, -6.28) * mm});
            skLineSegment(sketch, "E7.3.0.141", {"start": v(18, -11.55) * mm, "end": v(28, -11.55) * mm, "construction": true});
            skLineSegment(sketch, "E7.3.0.142", {"start": v(32, 11.55) * mm, "end": v(32, 9.55) * mm});
            skLineSegment(sketch, "E7.3.0.143", {"start": v(18, -9.55) * mm, "end": v(22, -9.55) * mm});
            skLineSegment(sketch, "E7.3.0.144", {"start": v(58, 11.55) * mm, "end": v(58, 9.55) * mm});
            skLineSegment(sketch, "E7.3.0.145", {"start": v(48, -4.28) * mm, "end": v(52, -4.28) * mm});
            skLineSegment(sketch, "E7.3.0.146", {"start": v(52, 9.55) * mm, "end": v(52, 4.27) * mm, "construction": true});
            skLineSegment(sketch, "E7.3.0.147", {"start": v(38, 4.27) * mm, "end": v(42, 4.27) * mm});
            skLineSegment(sketch, "E7.3.0.148", {"start": v(28, 11.55) * mm, "end": v(28, 9.55) * mm});
            skLineSegment(sketch, "E7.3.0.149", {"start": v(22, -9.55) * mm, "end": v(22, -11.55) * mm});
            skLineSegment(sketch, "E7.3.0.150", {"start": v(58, 9.55) * mm, "end": v(62, 9.55) * mm});
            skLineSegment(sketch, "E7.3.0.151", {"start": v(48, -4.28) * mm, "end": v(48, -6.28) * mm});
            skLineSegment(sketch, "E7.3.0.152", {"start": v(48, -1) * mm, "end": v(52, -1) * mm});
            skLineSegment(sketch, "E7.3.0.153", {"start": v(88, -6.28) * mm, "end": v(92, -6.28) * mm});
            skLineSegment(sketch, "E7.3.0.154", {"start": v(88, -9.55) * mm, "end": v(88, -11.55) * mm});
            skLineSegment(sketch, "E7.3.0.155", {"start": v(18, -4.28) * mm, "end": v(18, -6.28) * mm});
            skLineSegment(sketch, "E7.3.0.156", {"start": v(18, -4.28) * mm, "end": v(22, -4.28) * mm});
            skLineSegment(sketch, "E7.3.0.157", {"start": v(22, -4.28) * mm, "end": v(22, -6.28) * mm});
            skLineSegment(sketch, "E7.3.0.158", {"start": v(22, 6.27) * mm, "end": v(22, 4.27) * mm});
            skLineSegment(sketch, "E7.3.0.159", {"start": v(18, 1) * mm, "end": v(18, -1) * mm});
            skLineSegment(sketch, "E7.3.0.160", {"start": v(18, 1) * mm, "end": v(22, 1) * mm});
            skLineSegment(sketch, "E7.3.0.161", {"start": v(28, 9.55) * mm, "end": v(32, 9.55) * mm});
            skLineSegment(sketch, "E7.3.0.162", {"start": v(18, -11.55) * mm, "end": v(22, -11.55) * mm});
            skLineSegment(sketch, "E7.3.0.163", {"start": v(18, -1) * mm, "end": v(22, -1) * mm});
            skLineSegment(sketch, "E7.3.0.164", {"start": v(58, -6.28) * mm, "end": v(62, -6.28) * mm});
            skLineSegment(sketch, "E7.3.0.165", {"start": v(58, -9.55) * mm, "end": v(58, -11.55) * mm});
            skLineSegment(sketch, "E7.3.0.166", {"start": v(92, -9.55) * mm, "end": v(92, -11.55) * mm});
            skLineSegment(sketch, "E7.3.0.167", {"start": v(38, 6.27) * mm, "end": v(42, 6.27) * mm});
            skLineSegment(sketch, "E7.3.0.168", {"start": v(28, -6.28) * mm, "end": v(32, -6.28) * mm});
            skLineSegment(sketch, "E7.3.0.169", {"start": v(28, -9.55) * mm, "end": v(28, -11.55) * mm});
            skLineSegment(sketch, "E7.3.0.170", {"start": v(58, 11.55) * mm, "end": v(62, 11.55) * mm});
            skLineSegment(sketch, "E7.3.0.171", {"start": v(62, -9.55) * mm, "end": v(62, -11.55) * mm});
            skLineSegment(sketch, "E7.3.0.172", {"start": v(52, 1) * mm, "end": v(52, -1) * mm});
            skLineSegment(sketch, "E7.3.0.173", {"start": v(88, -9.55) * mm, "end": v(92, -9.55) * mm});
            skLineSegment(sketch, "E7.3.0.174", {"start": v(92, 9.55) * mm, "end": v(92, 4.27) * mm, "construction": true});
            skLineSegment(sketch, "E7.3.0.175", {"start": v(78, 1) * mm, "end": v(78, -1) * mm});
            skLineSegment(sketch, "E7.3.0.176", {"start": v(58, -4.28) * mm, "end": v(58, -6.28) * mm});
            skLineSegment(sketch, "E7.3.0.177", {"start": v(28, -1) * mm, "end": v(32, -1) * mm});
            skLineSegment(sketch, "E7.3.0.178", {"start": v(28, -4.28) * mm, "end": v(28, -6.28) * mm});
            skLineSegment(sketch, "E7.3.0.179", {"start": v(32, 1) * mm, "end": v(32, -1) * mm});
            skLineSegment(sketch, "E7.3.0.180", {"start": v(102, 9.55) * mm, "end": v(102, 4.27) * mm, "construction": true});
            skLineSegment(sketch, "E7.3.0.181", {"start": v(42, 9.55) * mm, "end": v(42, 4.27) * mm, "construction": true});
            skLineSegment(sketch, "E7.3.0.182", {"start": v(28, 1) * mm, "end": v(28, -1) * mm});
            skLineSegment(sketch, "E7.3.0.183", {"start": v(92, 6.27) * mm, "end": v(92, 4.27) * mm});
            skLineSegment(sketch, "E7.3.0.184", {"start": v(68, -4.28) * mm, "end": v(68, -6.28) * mm});
            skLineSegment(sketch, "E7.3.0.185", {"start": v(28, 1) * mm, "end": v(32, 1) * mm});
            skLineSegment(sketch, "E7.3.0.186", {"start": v(58, 1) * mm, "end": v(58, -1) * mm});
            skLineSegment(sketch, "E7.3.0.187", {"start": v(42, -4.28) * mm, "end": v(42, -6.28) * mm});
            skLineSegment(sketch, "E7.3.0.188", {"start": v(72, 9.55) * mm, "end": v(72, 4.27) * mm, "construction": true});
            skLineSegment(sketch, "E7.3.0.189", {"start": v(98, -4.28) * mm, "end": v(98, -6.28) * mm});
            skLineSegment(sketch, "E7.3.0.190", {"start": v(98, 4.27) * mm, "end": v(102, 4.27) * mm});
            skLineSegment(sketch, "E7.3.0.191", {"start": v(108, -1) * mm, "end": v(112, -1) * mm});
            skLineSegment(sketch, "E7.3.0.192", {"start": v(102, 6.27) * mm, "end": v(102, 4.27) * mm});
            skLineSegment(sketch, "E7.3.0.193", {"start": v(78, -1) * mm, "end": v(82, -1) * mm});
            skLineSegment(sketch, "E7.3.0.194", {"start": v(68, 4.27) * mm, "end": v(72, 4.27) * mm});
            skLineSegment(sketch, "E7.3.0.195", {"start": v(112, 1) * mm, "end": v(112, -1) * mm});
            skLineSegment(sketch, "E7.3.0.196", {"start": v(72, 6.27) * mm, "end": v(72, 4.27) * mm});
            skLineSegment(sketch, "E7.3.0.197", {"start": v(98, 6.27) * mm, "end": v(102, 6.27) * mm});
            skLineSegment(sketch, "E7.3.0.198", {"start": v(22, 11.55) * mm, "end": v(22, 9.55) * mm});
            skLineSegment(sketch, "E7.3.0.199", {"start": v(22, 1) * mm, "end": v(22, -1) * mm});
            skLineSegment(sketch, "E7.3.0.200", {"start": v(42, 6.27) * mm, "end": v(42, 4.27) * mm});
            skLineSegment(sketch, "E7.3.0.201", {"start": v(68, 6.27) * mm, "end": v(72, 6.27) * mm});
            skLineSegment(sketch, "E7.3.0.202", {"start": v(22, 9.55) * mm, "end": v(22, 4.27) * mm, "construction": true});
            skLineSegment(sketch, "E7.3.0.203", {"start": v(98, 6.27) * mm, "end": v(98, 4.27) * mm});
            skLineSegment(sketch, "E7.3.0.204", {"start": v(82, 1) * mm, "end": v(82, -1) * mm});
            skLineSegment(sketch, "E7.3.0.205", {"start": v(108, 1) * mm, "end": v(112, 1) * mm});
            skLineSegment(sketch, "E7.3.0.206", {"start": v(68, 6.27) * mm, "end": v(68, 4.27) * mm});
            skLineSegment(sketch, "E7.3.0.207", {"start": v(102, 11.55) * mm, "end": v(102, 9.55) * mm});
            skLineSegment(sketch, "E7.3.0.208", {"start": v(92, -4.28) * mm, "end": v(92, -6.28) * mm});
            skLineSegment(sketch, "E7.3.0.209", {"start": v(78, 1) * mm, "end": v(82, 1) * mm});
            skLineSegment(sketch, "E7.3.0.210", {"start": v(108, 1) * mm, "end": v(108, -1) * mm});
            skLineSegment(sketch, "E7.4.0.0", {"start": v(128, -9.55) * mm, "end": v(132, -9.55) * mm});
            skLineSegment(sketch, "E7.4.0.1", {"start": v(132, -9.55) * mm, "end": v(132, -11.55) * mm});
            skLineSegment(sketch, "E7.4.0.2", {"start": v(198, 11.55) * mm, "end": v(198, 9.55) * mm});
            skLineSegment(sketch, "E7.4.0.3", {"start": v(188, -1) * mm, "end": v(192, -1) * mm});
            skLineSegment(sketch, "E7.4.0.4", {"start": v(168, 11.55) * mm, "end": v(168, 9.55) * mm});
            skLineSegment(sketch, "E7.4.0.5", {"start": v(198, 9.55) * mm, "end": v(202, 9.55) * mm});
            skLineSegment(sketch, "E7.4.0.6", {"start": v(138, 11.55) * mm, "end": v(138, 9.55) * mm});
            skLineSegment(sketch, "E7.4.0.7", {"start": v(168, 9.55) * mm, "end": v(172, 9.55) * mm});
            skLineSegment(sketch, "E7.4.0.8", {"start": v(198, -9.55) * mm, "end": v(198, -11.55) * mm});
            skLineSegment(sketch, "E7.4.0.9", {"start": v(138, 9.55) * mm, "end": v(142, 9.55) * mm});
            skLineSegment(sketch, "E7.4.0.10", {"start": v(192, 1) * mm, "end": v(192, -1) * mm});
            skLineSegment(sketch, "E7.4.0.11", {"start": v(208, 6.27) * mm, "end": v(208, 4.27) * mm});
            skLineSegment(sketch, "E7.4.0.12", {"start": v(198, 11.55) * mm, "end": v(202, 11.55) * mm});
            skLineSegment(sketch, "E7.4.0.13", {"start": v(202, -9.55) * mm, "end": v(202, -11.55) * mm});
            skLineSegment(sketch, "E7.4.0.14", {"start": v(128, -11.55) * mm, "end": v(132, -11.55) * mm});
            skLineSegment(sketch, "E7.4.0.15", {"start": v(188, 1) * mm, "end": v(192, 1) * mm});
            skLineSegment(sketch, "E7.4.0.16", {"start": v(168, 11.55) * mm, "end": v(172, 11.55) * mm});
            skLineSegment(sketch, "E7.4.0.17", {"start": v(172, -9.55) * mm, "end": v(172, -11.55) * mm});
            skLineSegment(sketch, "E7.4.0.18", {"start": v(198, -9.55) * mm, "end": v(202, -9.55) * mm});
            skLineSegment(sketch, "E7.4.0.19", {"start": v(138, 11.55) * mm, "end": v(142, 11.55) * mm});
            skLineSegment(sketch, "E7.4.0.20", {"start": v(168, -9.55) * mm, "end": v(172, -9.55) * mm});
            skLineSegment(sketch, "E7.4.0.21", {"start": v(168, -1) * mm, "end": v(172, -1) * mm});
            skLineSegment(sketch, "E7.4.0.22", {"start": v(198, -11.55) * mm, "end": v(202, -11.55) * mm});
            skLineSegment(sketch, "E7.4.0.23", {"start": v(138, -1) * mm, "end": v(142, -1) * mm});
            skLineSegment(sketch, "E7.4.0.24", {"start": v(168, -11.55) * mm, "end": v(172, -11.55) * mm});
            skLineSegment(sketch, "E7.4.0.25", {"start": v(178, -9.55) * mm, "end": v(178, -11.55) * mm});
            skLineSegment(sketch, "E7.4.0.26", {"start": v(212, -9.55) * mm, "end": v(212, -11.55) * mm});
            skLineSegment(sketch, "E7.4.0.27", {"start": v(172, 1) * mm, "end": v(172, -1) * mm});
            skLineSegment(sketch, "E7.4.0.28", {"start": v(148, -9.55) * mm, "end": v(148, -11.55) * mm});
            skLineSegment(sketch, "E7.4.0.29", {"start": v(182, -9.55) * mm, "end": v(182, -11.55) * mm});
            skLineSegment(sketch, "E7.4.0.30", {"start": v(208, -9.55) * mm, "end": v(212, -9.55) * mm});
            skLineSegment(sketch, "E7.4.0.31", {"start": v(168, 1) * mm, "end": v(172, 1) * mm});
            skLineSegment(sketch, "E7.4.0.32", {"start": v(152, -9.55) * mm, "end": v(152, -11.55) * mm});
            skLineSegment(sketch, "E7.4.0.33", {"start": v(178, -9.55) * mm, "end": v(182, -9.55) * mm});
            skLineSegment(sketch, "E7.4.0.34", {"start": v(148, -9.55) * mm, "end": v(152, -9.55) * mm});
            skLineSegment(sketch, "E7.4.0.35", {"start": v(188, 11.55) * mm, "end": v(188, 9.55) * mm});
            skLineSegment(sketch, "E7.4.0.36", {"start": v(128, 6.27) * mm, "end": v(128, 4.27) * mm});
            skLineSegment(sketch, "E7.4.0.37", {"start": v(188, 9.55) * mm, "end": v(192, 9.55) * mm});
            skLineSegment(sketch, "E7.4.0.38", {"start": v(208, -11.55) * mm, "end": v(212, -11.55) * mm});
            skLineSegment(sketch, "E7.4.0.39", {"start": v(138, 1) * mm, "end": v(138, -1) * mm});
            skLineSegment(sketch, "E7.4.0.40", {"start": v(178, -11.55) * mm, "end": v(182, -11.55) * mm});
            skLineSegment(sketch, "E7.4.0.41", {"start": v(118, 11.55) * mm, "end": v(122, 11.55) * mm});
            skLineSegment(sketch, "E7.4.0.42", {"start": v(118, 9.55) * mm, "end": v(122, 9.55) * mm});
            skLineSegment(sketch, "E7.4.0.43", {"start": v(118, 11.55) * mm, "end": v(118, 9.55) * mm});
            skLineSegment(sketch, "E7.4.0.44", {"start": v(118, 6.27) * mm, "end": v(118, 4.27) * mm});
            skLineSegment(sketch, "E7.4.0.45", {"start": v(118, 6.27) * mm, "end": v(122, 6.27) * mm});
            skLineSegment(sketch, "E7.4.0.46", {"start": v(118, 4.27) * mm, "end": v(122, 4.27) * mm});
            skLineSegment(sketch, "E7.4.0.47", {"start": v(148, -11.55) * mm, "end": v(152, -11.55) * mm});
            skLineSegment(sketch, "E7.4.0.48", {"start": v(188, 11.55) * mm, "end": v(192, 11.55) * mm});
            skLineSegment(sketch, "E7.4.0.49", {"start": v(138, 6.27) * mm, "end": v(138, 4.27) * mm});
            skLineSegment(sketch, "E7.4.0.50", {"start": v(128, 11.55) * mm, "end": v(132, 11.55) * mm});
            skLineSegment(sketch, "E7.4.0.51", {"start": v(172, 11.55) * mm, "end": v(172, 9.55) * mm});
            skLineSegment(sketch, "E7.4.0.52", {"start": v(162, -4.28) * mm, "end": v(162, -6.28) * mm});
            skLineSegment(sketch, "E7.4.0.53", {"start": v(158, -9.55) * mm, "end": v(162, -9.55) * mm});
            skLineSegment(sketch, "E7.4.0.54", {"start": v(148, 1) * mm, "end": v(152, 1) * mm});
            skLineSegment(sketch, "E7.4.0.55", {"start": v(188, -4.28) * mm, "end": v(192, -4.28) * mm});
            skLineSegment(sketch, "E7.4.0.56", {"start": v(208, 4.27) * mm, "end": v(212, 4.27) * mm});
            skLineSegment(sketch, "E7.4.0.57", {"start": v(162, 9.55) * mm, "end": v(162, 4.27) * mm, "construction": true});
            skLineSegment(sketch, "E7.4.0.58", {"start": v(148, 1) * mm, "end": v(148, -1) * mm});
            skLineSegment(sketch, "E7.4.0.59", {"start": v(142, 11.55) * mm, "end": v(142, 9.55) * mm});
            skLineSegment(sketch, "E7.4.0.60", {"start": v(132, -4.28) * mm, "end": v(132, -6.28) * mm});
            skLineSegment(sketch, "E7.4.0.61", {"start": v(178, 4.27) * mm, "end": v(182, 4.27) * mm});
            skLineSegment(sketch, "E7.4.0.62", {"start": v(158, -4.28) * mm, "end": v(162, -4.28) * mm});
            skLineSegment(sketch, "E7.4.0.63", {"start": v(212, 6.27) * mm, "end": v(212, 4.27) * mm});
            skLineSegment(sketch, "E7.4.0.64", {"start": v(188, -4.28) * mm, "end": v(188, -6.28) * mm});
            skLineSegment(sketch, "E7.4.0.65", {"start": v(132, 9.55) * mm, "end": v(132, 4.27) * mm, "construction": true});
            skLineSegment(sketch, "E7.4.0.66", {"start": v(158, -1) * mm, "end": v(162, -1) * mm});
            skLineSegment(sketch, "E7.4.0.67", {"start": v(148, 4.27) * mm, "end": v(152, 4.27) * mm});
            skLineSegment(sketch, "E7.4.0.68", {"start": v(128, -4.28) * mm, "end": v(132, -4.28) * mm});
            skLineSegment(sketch, "E7.4.0.69", {"start": v(188, -11.55) * mm, "end": v(192, -11.55) * mm});
            skLineSegment(sketch, "E7.4.0.70", {"start": v(182, 6.27) * mm, "end": v(182, 4.27) * mm});
            skLineSegment(sketch, "E7.4.0.71", {"start": v(208, 6.27) * mm, "end": v(212, 6.27) * mm});
            skLineSegment(sketch, "E7.4.0.72", {"start": v(198, -6.28) * mm, "end": v(202, -6.28) * mm});
            skLineSegment(sketch, "E7.4.0.73", {"start": v(158, -11.55) * mm, "end": v(162, -11.55) * mm});
            skLineSegment(sketch, "E7.4.0.74", {"start": v(152, 6.27) * mm, "end": v(152, 4.27) * mm});
            skLineSegment(sketch, "E7.4.0.75", {"start": v(178, 6.27) * mm, "end": v(182, 6.27) * mm});
            skLineSegment(sketch, "E7.4.0.76", {"start": v(168, -6.28) * mm, "end": v(172, -6.28) * mm});
            skLineSegment(sketch, "E7.4.0.77", {"start": v(168, -9.55) * mm, "end": v(168, -11.55) * mm});
            skLineSegment(sketch, "E7.4.0.78", {"start": v(162, 1) * mm, "end": v(162, -1) * mm});
            skLineSegment(sketch, "E7.4.0.79", {"start": v(148, 6.27) * mm, "end": v(152, 6.27) * mm});
            skLineSegment(sketch, "E7.4.0.80", {"start": v(138, -6.28) * mm, "end": v(142, -6.28) * mm});
            skLineSegment(sketch, "E7.4.0.81", {"start": v(138, -9.55) * mm, "end": v(138, -11.55) * mm});
            skLineSegment(sketch, "E7.4.0.82", {"start": v(178, 6.27) * mm, "end": v(178, 4.27) * mm});
            skLineSegment(sketch, "E7.4.0.83", {"start": v(212, 11.55) * mm, "end": v(212, 9.55) * mm});
            skLineSegment(sketch, "E7.4.0.84", {"start": v(202, -4.28) * mm, "end": v(202, -6.28) * mm});
            skLineSegment(sketch, "E7.4.0.85", {"start": v(158, 1) * mm, "end": v(162, 1) * mm});
            skLineSegment(sketch, "E7.4.0.86", {"start": v(148, 6.27) * mm, "end": v(148, 4.27) * mm});
            skLineSegment(sketch, "E7.4.0.87", {"start": v(142, -9.55) * mm, "end": v(142, -11.55) * mm});
            skLineSegment(sketch, "E7.4.0.88", {"start": v(188, 1) * mm, "end": v(188, -1) * mm});
            skLineSegment(sketch, "E7.4.0.89", {"start": v(182, 11.55) * mm, "end": v(182, 9.55) * mm});
            skLineSegment(sketch, "E7.4.0.90", {"start": v(172, -4.28) * mm, "end": v(172, -6.28) * mm});
            skLineSegment(sketch, "E7.4.0.91", {"start": v(208, 11.55) * mm, "end": v(208, 9.55) * mm});
            skLineSegment(sketch, "E7.4.0.92", {"start": v(198, -4.28) * mm, "end": v(202, -4.28) * mm});
            skLineSegment(sketch, "E7.4.0.93", {"start": v(158, 4.27) * mm, "end": v(162, 4.27) * mm});
            skLineSegment(sketch, "E7.4.0.94", {"start": v(148, 11.55) * mm, "end": v(148, 9.55) * mm});
            skLineSegment(sketch, "E7.4.0.95", {"start": v(138, -4.28) * mm, "end": v(142, -4.28) * mm});
            skLineSegment(sketch, "E7.4.0.96", {"start": v(178, 9.55) * mm, "end": v(182, 9.55) * mm});
            skLineSegment(sketch, "E7.4.0.97", {"start": v(208, -6.28) * mm, "end": v(212, -6.28) * mm});
            skLineSegment(sketch, "E7.4.0.98", {"start": v(208, -9.55) * mm, "end": v(208, -11.55) * mm});
            skLineSegment(sketch, "E7.4.0.99", {"start": v(152, 11.55) * mm, "end": v(152, 9.55) * mm});
            skLineSegment(sketch, "E7.4.0.100", {"start": v(138, -9.55) * mm, "end": v(142, -9.55) * mm});
            skLineSegment(sketch, "E7.4.0.101", {"start": v(188, 4.27) * mm, "end": v(192, 4.27) * mm});
            skLineSegment(sketch, "E7.4.0.102", {"start": v(178, 11.55) * mm, "end": v(178, 9.55) * mm});
            skLineSegment(sketch, "E7.4.0.103", {"start": v(168, -4.28) * mm, "end": v(172, -4.28) * mm});
            skLineSegment(sketch, "E7.4.0.104", {"start": v(208, 9.55) * mm, "end": v(212, 9.55) * mm});
            skLineSegment(sketch, "E7.4.0.105", {"start": v(198, -1) * mm, "end": v(202, -1) * mm});
            skLineSegment(sketch, "E7.4.0.106", {"start": v(128, 4.27) * mm, "end": v(132, 4.27) * mm});
            skLineSegment(sketch, "E7.4.0.107", {"start": v(162, 6.27) * mm, "end": v(162, 4.27) * mm});
            skLineSegment(sketch, "E7.4.0.108", {"start": v(148, 9.55) * mm, "end": v(152, 9.55) * mm});
            skLineSegment(sketch, "E7.4.0.109", {"start": v(138, -4.28) * mm, "end": v(138, -6.28) * mm});
            skLineSegment(sketch, "E7.4.0.110", {"start": v(202, 1) * mm, "end": v(202, -1) * mm});
            skLineSegment(sketch, "E7.4.0.111", {"start": v(188, 6.27) * mm, "end": v(192, 6.27) * mm});
            skLineSegment(sketch, "E7.4.0.112", {"start": v(178, -6.28) * mm, "end": v(182, -6.28) * mm});
            skLineSegment(sketch, "E7.4.0.113", {"start": v(208, 11.55) * mm, "end": v(212, 11.55) * mm});
            skLineSegment(sketch, "E7.4.0.114", {"start": v(138, -11.55) * mm, "end": v(142, -11.55) * mm});
            skLineSegment(sketch, "E7.4.0.115", {"start": v(132, 6.27) * mm, "end": v(132, 4.27) * mm});
            skLineSegment(sketch, "E7.4.0.116", {"start": v(158, 6.27) * mm, "end": v(162, 6.27) * mm});
            skLineSegment(sketch, "E7.4.0.117", {"start": v(148, -6.28) * mm, "end": v(152, -6.28) * mm});
            skLineSegment(sketch, "E7.4.0.118", {"start": v(198, 1) * mm, "end": v(202, 1) * mm});
            skLineSegment(sketch, "E7.4.0.119", {"start": v(188, 6.27) * mm, "end": v(188, 4.27) * mm});
            skLineSegment(sketch, "E7.4.0.120", {"start": v(178, 11.55) * mm, "end": v(182, 11.55) * mm});
            skLineSegment(sketch, "E7.4.0.121", {"start": v(212, -4.28) * mm, "end": v(212, -6.28) * mm});
            skLineSegment(sketch, "E7.4.0.122", {"start": v(142, 1) * mm, "end": v(142, -1) * mm});
            skLineSegment(sketch, "E7.4.0.123", {"start": v(128, 6.27) * mm, "end": v(132, 6.27) * mm});
            skLineSegment(sketch, "E7.4.0.124", {"start": v(118, -6.28) * mm, "end": v(122, -6.28) * mm});
            skLineSegment(sketch, "E7.4.0.125", {"start": v(158, 6.27) * mm, "end": v(158, 4.27) * mm});
            skLineSegment(sketch, "E7.4.0.126", {"start": v(148, 11.55) * mm, "end": v(152, 11.55) * mm});
            skLineSegment(sketch, "E7.4.0.127", {"start": v(198, 1) * mm, "end": v(198, -1) * mm});
            skLineSegment(sketch, "E7.4.0.128", {"start": v(192, 11.55) * mm, "end": v(192, 9.55) * mm});
            skLineSegment(sketch, "E7.4.0.129", {"start": v(182, -4.28) * mm, "end": v(182, -6.28) * mm});
            skLineSegment(sketch, "E7.4.0.130", {"start": v(208, -4.28) * mm, "end": v(212, -4.28) * mm});
            skLineSegment(sketch, "E7.4.0.131", {"start": v(212, 9.55) * mm, "end": v(212, 4.27) * mm, "construction": true});
            skLineSegment(sketch, "E7.4.0.132", {"start": v(168, 1) * mm, "end": v(168, -1) * mm});
            skLineSegment(sketch, "E7.4.0.133", {"start": v(162, 11.55) * mm, "end": v(162, 9.55) * mm});
            skLineSegment(sketch, "E7.4.0.134", {"start": v(152, -4.28) * mm, "end": v(152, -6.28) * mm});
            skLineSegment(sketch, "E7.4.0.135", {"start": v(178, -4.28) * mm, "end": v(182, -4.28) * mm});
            skLineSegment(sketch, "E7.4.0.136", {"start": v(182, 9.55) * mm, "end": v(182, 4.27) * mm, "construction": true});
            skLineSegment(sketch, "E7.4.0.137", {"start": v(208, -4.28) * mm, "end": v(208, -6.28) * mm});
            skLineSegment(sketch, "E7.4.0.138", {"start": v(138, 1) * mm, "end": v(142, 1) * mm});
            skLineSegment(sketch, "E7.4.0.139", {"start": v(118, -9.55) * mm, "end": v(118, -11.55) * mm});
            skLineSegment(sketch, "E7.4.0.140", {"start": v(178, -4.28) * mm, "end": v(178, -6.28) * mm});
            skLineSegment(sketch, "E7.4.0.141", {"start": v(118, -11.55) * mm, "end": v(128, -11.55) * mm, "construction": true});
            skLineSegment(sketch, "E7.4.0.142", {"start": v(132, 11.55) * mm, "end": v(132, 9.55) * mm});
            skLineSegment(sketch, "E7.4.0.143", {"start": v(118, -9.55) * mm, "end": v(122, -9.55) * mm});
            skLineSegment(sketch, "E7.4.0.144", {"start": v(158, 11.55) * mm, "end": v(158, 9.55) * mm});
            skLineSegment(sketch, "E7.4.0.145", {"start": v(148, -4.28) * mm, "end": v(152, -4.28) * mm});
            skLineSegment(sketch, "E7.4.0.146", {"start": v(152, 9.55) * mm, "end": v(152, 4.27) * mm, "construction": true});
            skLineSegment(sketch, "E7.4.0.147", {"start": v(138, 4.27) * mm, "end": v(142, 4.27) * mm});
            skLineSegment(sketch, "E7.4.0.148", {"start": v(128, 11.55) * mm, "end": v(128, 9.55) * mm});
            skLineSegment(sketch, "E7.4.0.149", {"start": v(122, -9.55) * mm, "end": v(122, -11.55) * mm});
            skLineSegment(sketch, "E7.4.0.150", {"start": v(158, 9.55) * mm, "end": v(162, 9.55) * mm});
            skLineSegment(sketch, "E7.4.0.151", {"start": v(148, -4.28) * mm, "end": v(148, -6.28) * mm});
            skLineSegment(sketch, "E7.4.0.152", {"start": v(148, -1) * mm, "end": v(152, -1) * mm});
            skLineSegment(sketch, "E7.4.0.153", {"start": v(188, -6.28) * mm, "end": v(192, -6.28) * mm});
            skLineSegment(sketch, "E7.4.0.154", {"start": v(188, -9.55) * mm, "end": v(188, -11.55) * mm});
            skLineSegment(sketch, "E7.4.0.155", {"start": v(118, -4.28) * mm, "end": v(118, -6.28) * mm});
            skLineSegment(sketch, "E7.4.0.156", {"start": v(118, -4.28) * mm, "end": v(122, -4.28) * mm});
            skLineSegment(sketch, "E7.4.0.157", {"start": v(122, -4.28) * mm, "end": v(122, -6.28) * mm});
            skLineSegment(sketch, "E7.4.0.158", {"start": v(122, 6.27) * mm, "end": v(122, 4.27) * mm});
            skLineSegment(sketch, "E7.4.0.159", {"start": v(118, 1) * mm, "end": v(118, -1) * mm});
            skLineSegment(sketch, "E7.4.0.160", {"start": v(118, 1) * mm, "end": v(122, 1) * mm});
            skLineSegment(sketch, "E7.4.0.161", {"start": v(128, 9.55) * mm, "end": v(132, 9.55) * mm});
            skLineSegment(sketch, "E7.4.0.162", {"start": v(118, -11.55) * mm, "end": v(122, -11.55) * mm});
            skLineSegment(sketch, "E7.4.0.163", {"start": v(118, -1) * mm, "end": v(122, -1) * mm});
            skLineSegment(sketch, "E7.4.0.164", {"start": v(158, -6.28) * mm, "end": v(162, -6.28) * mm});
            skLineSegment(sketch, "E7.4.0.165", {"start": v(158, -9.55) * mm, "end": v(158, -11.55) * mm});
            skLineSegment(sketch, "E7.4.0.166", {"start": v(192, -9.55) * mm, "end": v(192, -11.55) * mm});
            skLineSegment(sketch, "E7.4.0.167", {"start": v(138, 6.27) * mm, "end": v(142, 6.27) * mm});
            skLineSegment(sketch, "E7.4.0.168", {"start": v(128, -6.28) * mm, "end": v(132, -6.28) * mm});
            skLineSegment(sketch, "E7.4.0.169", {"start": v(128, -9.55) * mm, "end": v(128, -11.55) * mm});
            skLineSegment(sketch, "E7.4.0.170", {"start": v(158, 11.55) * mm, "end": v(162, 11.55) * mm});
            skLineSegment(sketch, "E7.4.0.171", {"start": v(162, -9.55) * mm, "end": v(162, -11.55) * mm});
            skLineSegment(sketch, "E7.4.0.172", {"start": v(152, 1) * mm, "end": v(152, -1) * mm});
            skLineSegment(sketch, "E7.4.0.173", {"start": v(188, -9.55) * mm, "end": v(192, -9.55) * mm});
            skLineSegment(sketch, "E7.4.0.174", {"start": v(192, 9.55) * mm, "end": v(192, 4.27) * mm, "construction": true});
            skLineSegment(sketch, "E7.4.0.175", {"start": v(178, 1) * mm, "end": v(178, -1) * mm});
            skLineSegment(sketch, "E7.4.0.176", {"start": v(158, -4.28) * mm, "end": v(158, -6.28) * mm});
            skLineSegment(sketch, "E7.4.0.177", {"start": v(128, -1) * mm, "end": v(132, -1) * mm});
            skLineSegment(sketch, "E7.4.0.178", {"start": v(128, -4.28) * mm, "end": v(128, -6.28) * mm});
            skLineSegment(sketch, "E7.4.0.179", {"start": v(132, 1) * mm, "end": v(132, -1) * mm});
            skLineSegment(sketch, "E7.4.0.180", {"start": v(202, 9.55) * mm, "end": v(202, 4.27) * mm, "construction": true});
            skLineSegment(sketch, "E7.4.0.181", {"start": v(142, 9.55) * mm, "end": v(142, 4.27) * mm, "construction": true});
            skLineSegment(sketch, "E7.4.0.182", {"start": v(128, 1) * mm, "end": v(128, -1) * mm});
            skLineSegment(sketch, "E7.4.0.183", {"start": v(192, 6.27) * mm, "end": v(192, 4.27) * mm});
            skLineSegment(sketch, "E7.4.0.184", {"start": v(168, -4.28) * mm, "end": v(168, -6.28) * mm});
            skLineSegment(sketch, "E7.4.0.185", {"start": v(128, 1) * mm, "end": v(132, 1) * mm});
            skLineSegment(sketch, "E7.4.0.186", {"start": v(158, 1) * mm, "end": v(158, -1) * mm});
            skLineSegment(sketch, "E7.4.0.187", {"start": v(142, -4.28) * mm, "end": v(142, -6.28) * mm});
            skLineSegment(sketch, "E7.4.0.188", {"start": v(172, 9.55) * mm, "end": v(172, 4.27) * mm, "construction": true});
            skLineSegment(sketch, "E7.4.0.189", {"start": v(198, -4.28) * mm, "end": v(198, -6.28) * mm});
            skLineSegment(sketch, "E7.4.0.190", {"start": v(198, 4.27) * mm, "end": v(202, 4.27) * mm});
            skLineSegment(sketch, "E7.4.0.191", {"start": v(208, -1) * mm, "end": v(212, -1) * mm});
            skLineSegment(sketch, "E7.4.0.192", {"start": v(202, 6.27) * mm, "end": v(202, 4.27) * mm});
            skLineSegment(sketch, "E7.4.0.193", {"start": v(178, -1) * mm, "end": v(182, -1) * mm});
            skLineSegment(sketch, "E7.4.0.194", {"start": v(168, 4.27) * mm, "end": v(172, 4.27) * mm});
            skLineSegment(sketch, "E7.4.0.195", {"start": v(212, 1) * mm, "end": v(212, -1) * mm});
            skLineSegment(sketch, "E7.4.0.196", {"start": v(172, 6.27) * mm, "end": v(172, 4.27) * mm});
            skLineSegment(sketch, "E7.4.0.197", {"start": v(198, 6.27) * mm, "end": v(202, 6.27) * mm});
            skLineSegment(sketch, "E7.4.0.198", {"start": v(122, 11.55) * mm, "end": v(122, 9.55) * mm});
            skLineSegment(sketch, "E7.4.0.199", {"start": v(122, 1) * mm, "end": v(122, -1) * mm});
            skLineSegment(sketch, "E7.4.0.200", {"start": v(142, 6.27) * mm, "end": v(142, 4.27) * mm});
            skLineSegment(sketch, "E7.4.0.201", {"start": v(168, 6.27) * mm, "end": v(172, 6.27) * mm});
            skLineSegment(sketch, "E7.4.0.202", {"start": v(122, 9.55) * mm, "end": v(122, 4.27) * mm, "construction": true});
            skLineSegment(sketch, "E7.4.0.203", {"start": v(198, 6.27) * mm, "end": v(198, 4.27) * mm});
            skLineSegment(sketch, "E7.4.0.204", {"start": v(182, 1) * mm, "end": v(182, -1) * mm});
            skLineSegment(sketch, "E7.4.0.205", {"start": v(208, 1) * mm, "end": v(212, 1) * mm});
            skLineSegment(sketch, "E7.4.0.206", {"start": v(168, 6.27) * mm, "end": v(168, 4.27) * mm});
            skLineSegment(sketch, "E7.4.0.207", {"start": v(202, 11.55) * mm, "end": v(202, 9.55) * mm});
            skLineSegment(sketch, "E7.4.0.208", {"start": v(192, -4.28) * mm, "end": v(192, -6.28) * mm});
            skLineSegment(sketch, "E7.4.0.209", {"start": v(178, 1) * mm, "end": v(182, 1) * mm});
            skLineSegment(sketch, "E7.4.0.210", {"start": v(208, 1) * mm, "end": v(208, -1) * mm});
            skLineSegment(sketch, "E7.5.0.0", {"start": v(228, -9.55) * mm, "end": v(232, -9.55) * mm});
            skLineSegment(sketch, "E7.5.0.1", {"start": v(232, -9.55) * mm, "end": v(232, -11.55) * mm});
            skLineSegment(sketch, "E7.5.0.4", {"start": v(268, 11.55) * mm, "end": v(268, 9.55) * mm});
            skLineSegment(sketch, "E7.5.0.6", {"start": v(238, 11.55) * mm, "end": v(238, 9.55) * mm});
            skLineSegment(sketch, "E7.5.0.7", {"start": v(268, 9.55) * mm, "end": v(272, 9.55) * mm});
            skLineSegment(sketch, "E7.5.0.9", {"start": v(238, 9.55) * mm, "end": v(242, 9.55) * mm});
            skLineSegment(sketch, "E7.5.0.14", {"start": v(228, -11.55) * mm, "end": v(232, -11.55) * mm});
            skLineSegment(sketch, "E7.5.0.16", {"start": v(268, 11.55) * mm, "end": v(272, 11.55) * mm});
            skLineSegment(sketch, "E7.5.0.17", {"start": v(272, -9.55) * mm, "end": v(272, -11.55) * mm});
            skLineSegment(sketch, "E7.5.0.19", {"start": v(238, 11.55) * mm, "end": v(242, 11.55) * mm});
            skLineSegment(sketch, "E7.5.0.20", {"start": v(268, -9.55) * mm, "end": v(272, -9.55) * mm});
            skLineSegment(sketch, "E7.5.0.21", {"start": v(268, -1) * mm, "end": v(272, -1) * mm});
            skLineSegment(sketch, "E7.5.0.23", {"start": v(238, -1) * mm, "end": v(242, -1) * mm});
            skLineSegment(sketch, "E7.5.0.24", {"start": v(268, -11.55) * mm, "end": v(272, -11.55) * mm});
            skLineSegment(sketch, "E7.5.0.25", {"start": v(278, -9.55) * mm, "end": v(278, -11.55) * mm});
            skLineSegment(sketch, "E7.5.0.27", {"start": v(272, 1) * mm, "end": v(272, -1) * mm});
            skLineSegment(sketch, "E7.5.0.28", {"start": v(248, -9.55) * mm, "end": v(248, -11.55) * mm});
            skLineSegment(sketch, "E7.5.0.29", {"start": v(282, -9.55) * mm, "end": v(282, -11.55) * mm});
            skLineSegment(sketch, "E7.5.0.31", {"start": v(268, 1) * mm, "end": v(272, 1) * mm});
            skLineSegment(sketch, "E7.5.0.32", {"start": v(252, -9.55) * mm, "end": v(252, -11.55) * mm});
            skLineSegment(sketch, "E7.5.0.33", {"start": v(278, -9.55) * mm, "end": v(282, -9.55) * mm});
            skLineSegment(sketch, "E7.5.0.34", {"start": v(248, -9.55) * mm, "end": v(252, -9.55) * mm});
            skLineSegment(sketch, "E7.5.0.36", {"start": v(228, 6.27) * mm, "end": v(228, 4.27) * mm});
            skLineSegment(sketch, "E7.5.0.39", {"start": v(238, 1) * mm, "end": v(238, -1) * mm});
            skLineSegment(sketch, "E7.5.0.40", {"start": v(278, -11.55) * mm, "end": v(282, -11.55) * mm});
            skLineSegment(sketch, "E7.5.0.41", {"start": v(218, 11.55) * mm, "end": v(222, 11.55) * mm});
            skLineSegment(sketch, "E7.5.0.42", {"start": v(218, 9.55) * mm, "end": v(222, 9.55) * mm});
            skLineSegment(sketch, "E7.5.0.43", {"start": v(218, 11.55) * mm, "end": v(218, 9.55) * mm});
            skLineSegment(sketch, "E7.5.0.44", {"start": v(218, 6.27) * mm, "end": v(218, 4.27) * mm});
            skLineSegment(sketch, "E7.5.0.45", {"start": v(218, 6.27) * mm, "end": v(222, 6.27) * mm});
            skLineSegment(sketch, "E7.5.0.46", {"start": v(218, 4.27) * mm, "end": v(222, 4.27) * mm});
            skLineSegment(sketch, "E7.5.0.47", {"start": v(248, -11.55) * mm, "end": v(252, -11.55) * mm});
            skLineSegment(sketch, "E7.5.0.49", {"start": v(238, 6.27) * mm, "end": v(238, 4.27) * mm});
            skLineSegment(sketch, "E7.5.0.50", {"start": v(228, 11.55) * mm, "end": v(232, 11.55) * mm});
            skLineSegment(sketch, "E7.5.0.51", {"start": v(272, 11.55) * mm, "end": v(272, 9.55) * mm});
            skLineSegment(sketch, "E7.5.0.52", {"start": v(262, -4.28) * mm, "end": v(262, -6.28) * mm});
            skLineSegment(sketch, "E7.5.0.53", {"start": v(258, -9.55) * mm, "end": v(262, -9.55) * mm});
            skLineSegment(sketch, "E7.5.0.54", {"start": v(248, 1) * mm, "end": v(252, 1) * mm});
            skLineSegment(sketch, "E7.5.0.57", {"start": v(262, 9.55) * mm, "end": v(262, 4.27) * mm, "construction": true});
            skLineSegment(sketch, "E7.5.0.58", {"start": v(248, 1) * mm, "end": v(248, -1) * mm});
            skLineSegment(sketch, "E7.5.0.59", {"start": v(242, 11.55) * mm, "end": v(242, 9.55) * mm});
            skLineSegment(sketch, "E7.5.0.60", {"start": v(232, -4.28) * mm, "end": v(232, -6.28) * mm});
            skLineSegment(sketch, "E7.5.0.61", {"start": v(278, 4.27) * mm, "end": v(282, 4.27) * mm});
            skLineSegment(sketch, "E7.5.0.62", {"start": v(258, -4.28) * mm, "end": v(262, -4.28) * mm});
            skLineSegment(sketch, "E7.5.0.65", {"start": v(232, 9.55) * mm, "end": v(232, 4.27) * mm, "construction": true});
            skLineSegment(sketch, "E7.5.0.66", {"start": v(258, -1) * mm, "end": v(262, -1) * mm});
            skLineSegment(sketch, "E7.5.0.67", {"start": v(248, 4.27) * mm, "end": v(252, 4.27) * mm});
            skLineSegment(sketch, "E7.5.0.68", {"start": v(228, -4.28) * mm, "end": v(232, -4.28) * mm});
            skLineSegment(sketch, "E7.5.0.70", {"start": v(282, 6.27) * mm, "end": v(282, 4.27) * mm});
            skLineSegment(sketch, "E7.5.0.73", {"start": v(258, -11.55) * mm, "end": v(262, -11.55) * mm});
            skLineSegment(sketch, "E7.5.0.74", {"start": v(252, 6.27) * mm, "end": v(252, 4.27) * mm});
            skLineSegment(sketch, "E7.5.0.75", {"start": v(278, 6.27) * mm, "end": v(282, 6.27) * mm});
            skLineSegment(sketch, "E7.5.0.76", {"start": v(268, -6.28) * mm, "end": v(272, -6.28) * mm});
            skLineSegment(sketch, "E7.5.0.77", {"start": v(268, -9.55) * mm, "end": v(268, -11.55) * mm});
            skLineSegment(sketch, "E7.5.0.78", {"start": v(262, 1) * mm, "end": v(262, -1) * mm});
            skLineSegment(sketch, "E7.5.0.79", {"start": v(248, 6.27) * mm, "end": v(252, 6.27) * mm});
            skLineSegment(sketch, "E7.5.0.80", {"start": v(238, -6.28) * mm, "end": v(242, -6.28) * mm});
            skLineSegment(sketch, "E7.5.0.81", {"start": v(238, -9.55) * mm, "end": v(238, -11.55) * mm});
            skLineSegment(sketch, "E7.5.0.82", {"start": v(278, 6.27) * mm, "end": v(278, 4.27) * mm});
            skLineSegment(sketch, "E7.5.0.85", {"start": v(258, 1) * mm, "end": v(262, 1) * mm});
            skLineSegment(sketch, "E7.5.0.86", {"start": v(248, 6.27) * mm, "end": v(248, 4.27) * mm});
            skLineSegment(sketch, "E7.5.0.87", {"start": v(242, -9.55) * mm, "end": v(242, -11.55) * mm});
            skLineSegment(sketch, "E7.5.0.89", {"start": v(282, 11.55) * mm, "end": v(282, 9.55) * mm});
            skLineSegment(sketch, "E7.5.0.90", {"start": v(272, -4.28) * mm, "end": v(272, -6.28) * mm});
            skLineSegment(sketch, "E7.5.0.93", {"start": v(258, 4.27) * mm, "end": v(262, 4.27) * mm});
            skLineSegment(sketch, "E7.5.0.94", {"start": v(248, 11.55) * mm, "end": v(248, 9.55) * mm});
            skLineSegment(sketch, "E7.5.0.95", {"start": v(238, -4.28) * mm, "end": v(242, -4.28) * mm});
            skLineSegment(sketch, "E7.5.0.96", {"start": v(278, 9.55) * mm, "end": v(282, 9.55) * mm});
            skLineSegment(sketch, "E7.5.0.99", {"start": v(252, 11.55) * mm, "end": v(252, 9.55) * mm});
            skLineSegment(sketch, "E7.5.0.100", {"start": v(238, -9.55) * mm, "end": v(242, -9.55) * mm});
            skLineSegment(sketch, "E7.5.0.102", {"start": v(278, 11.55) * mm, "end": v(278, 9.55) * mm});
            skLineSegment(sketch, "E7.5.0.103", {"start": v(268, -4.28) * mm, "end": v(272, -4.28) * mm});
            skLineSegment(sketch, "E7.5.0.106", {"start": v(228, 4.27) * mm, "end": v(232, 4.27) * mm});
            skLineSegment(sketch, "E7.5.0.107", {"start": v(262, 6.27) * mm, "end": v(262, 4.27) * mm});
            skLineSegment(sketch, "E7.5.0.108", {"start": v(248, 9.55) * mm, "end": v(252, 9.55) * mm});
            skLineSegment(sketch, "E7.5.0.109", {"start": v(238, -4.28) * mm, "end": v(238, -6.28) * mm});
            skLineSegment(sketch, "E7.5.0.112", {"start": v(278, -6.28) * mm, "end": v(282, -6.28) * mm});
            skLineSegment(sketch, "E7.5.0.114", {"start": v(238, -11.55) * mm, "end": v(242, -11.55) * mm});
            skLineSegment(sketch, "E7.5.0.115", {"start": v(232, 6.27) * mm, "end": v(232, 4.27) * mm});
            skLineSegment(sketch, "E7.5.0.116", {"start": v(258, 6.27) * mm, "end": v(262, 6.27) * mm});
            skLineSegment(sketch, "E7.5.0.117", {"start": v(248, -6.28) * mm, "end": v(252, -6.28) * mm});
            skLineSegment(sketch, "E7.5.0.120", {"start": v(278, 11.55) * mm, "end": v(282, 11.55) * mm});
            skLineSegment(sketch, "E7.5.0.122", {"start": v(242, 1) * mm, "end": v(242, -1) * mm});
            skLineSegment(sketch, "E7.5.0.123", {"start": v(228, 6.27) * mm, "end": v(232, 6.27) * mm});
            skLineSegment(sketch, "E7.5.0.124", {"start": v(218, -6.28) * mm, "end": v(222, -6.28) * mm});
            skLineSegment(sketch, "E7.5.0.125", {"start": v(258, 6.27) * mm, "end": v(258, 4.27) * mm});
            skLineSegment(sketch, "E7.5.0.126", {"start": v(248, 11.55) * mm, "end": v(252, 11.55) * mm});
            skLineSegment(sketch, "E7.5.0.129", {"start": v(282, -4.28) * mm, "end": v(282, -6.28) * mm});
            skLineSegment(sketch, "E7.5.0.132", {"start": v(268, 1) * mm, "end": v(268, -1) * mm});
            skLineSegment(sketch, "E7.5.0.133", {"start": v(262, 11.55) * mm, "end": v(262, 9.55) * mm});
            skLineSegment(sketch, "E7.5.0.134", {"start": v(252, -4.28) * mm, "end": v(252, -6.28) * mm});
            skLineSegment(sketch, "E7.5.0.135", {"start": v(278, -4.28) * mm, "end": v(282, -4.28) * mm});
            skLineSegment(sketch, "E7.5.0.136", {"start": v(282, 9.55) * mm, "end": v(282, 4.27) * mm, "construction": true});
            skLineSegment(sketch, "E7.5.0.138", {"start": v(238, 1) * mm, "end": v(242, 1) * mm});
            skLineSegment(sketch, "E7.5.0.139", {"start": v(218, -9.55) * mm, "end": v(218, -11.55) * mm});
            skLineSegment(sketch, "E7.5.0.140", {"start": v(278, -4.28) * mm, "end": v(278, -6.28) * mm});
            skLineSegment(sketch, "E7.5.0.141", {"start": v(218, -11.55) * mm, "end": v(228, -11.55) * mm, "construction": true});
            skLineSegment(sketch, "E7.5.0.142", {"start": v(232, 11.55) * mm, "end": v(232, 9.55) * mm});
            skLineSegment(sketch, "E7.5.0.143", {"start": v(218, -9.55) * mm, "end": v(222, -9.55) * mm});
            skLineSegment(sketch, "E7.5.0.144", {"start": v(258, 11.55) * mm, "end": v(258, 9.55) * mm});
            skLineSegment(sketch, "E7.5.0.145", {"start": v(248, -4.28) * mm, "end": v(252, -4.28) * mm});
            skLineSegment(sketch, "E7.5.0.146", {"start": v(252, 9.55) * mm, "end": v(252, 4.27) * mm, "construction": true});
            skLineSegment(sketch, "E7.5.0.147", {"start": v(238, 4.27) * mm, "end": v(242, 4.27) * mm});
            skLineSegment(sketch, "E7.5.0.148", {"start": v(228, 11.55) * mm, "end": v(228, 9.55) * mm});
            skLineSegment(sketch, "E7.5.0.149", {"start": v(222, -9.55) * mm, "end": v(222, -11.55) * mm});
            skLineSegment(sketch, "E7.5.0.150", {"start": v(258, 9.55) * mm, "end": v(262, 9.55) * mm});
            skLineSegment(sketch, "E7.5.0.151", {"start": v(248, -4.28) * mm, "end": v(248, -6.28) * mm});
            skLineSegment(sketch, "E7.5.0.152", {"start": v(248, -1) * mm, "end": v(252, -1) * mm});
            skLineSegment(sketch, "E7.5.0.155", {"start": v(218, -4.28) * mm, "end": v(218, -6.28) * mm});
            skLineSegment(sketch, "E7.5.0.156", {"start": v(218, -4.28) * mm, "end": v(222, -4.28) * mm});
            skLineSegment(sketch, "E7.5.0.157", {"start": v(222, -4.28) * mm, "end": v(222, -6.28) * mm});
            skLineSegment(sketch, "E7.5.0.158", {"start": v(222, 6.27) * mm, "end": v(222, 4.27) * mm});
            skLineSegment(sketch, "E7.5.0.159", {"start": v(218, 1) * mm, "end": v(218, -1) * mm});
            skLineSegment(sketch, "E7.5.0.160", {"start": v(218, 1) * mm, "end": v(222, 1) * mm});
            skLineSegment(sketch, "E7.5.0.161", {"start": v(228, 9.55) * mm, "end": v(232, 9.55) * mm});
            skLineSegment(sketch, "E7.5.0.162", {"start": v(218, -11.55) * mm, "end": v(222, -11.55) * mm});
            skLineSegment(sketch, "E7.5.0.163", {"start": v(218, -1) * mm, "end": v(222, -1) * mm});
            skLineSegment(sketch, "E7.5.0.164", {"start": v(258, -6.28) * mm, "end": v(262, -6.28) * mm});
            skLineSegment(sketch, "E7.5.0.165", {"start": v(258, -9.55) * mm, "end": v(258, -11.55) * mm});
            skLineSegment(sketch, "E7.5.0.167", {"start": v(238, 6.27) * mm, "end": v(242, 6.27) * mm});
            skLineSegment(sketch, "E7.5.0.168", {"start": v(228, -6.28) * mm, "end": v(232, -6.28) * mm});
            skLineSegment(sketch, "E7.5.0.169", {"start": v(228, -9.55) * mm, "end": v(228, -11.55) * mm});
            skLineSegment(sketch, "E7.5.0.170", {"start": v(258, 11.55) * mm, "end": v(262, 11.55) * mm});
            skLineSegment(sketch, "E7.5.0.171", {"start": v(262, -9.55) * mm, "end": v(262, -11.55) * mm});
            skLineSegment(sketch, "E7.5.0.172", {"start": v(252, 1) * mm, "end": v(252, -1) * mm});
            skLineSegment(sketch, "E7.5.0.175", {"start": v(278, 1) * mm, "end": v(278, -1) * mm});
            skLineSegment(sketch, "E7.5.0.176", {"start": v(258, -4.28) * mm, "end": v(258, -6.28) * mm});
            skLineSegment(sketch, "E7.5.0.177", {"start": v(228, -1) * mm, "end": v(232, -1) * mm});
            skLineSegment(sketch, "E7.5.0.178", {"start": v(228, -4.28) * mm, "end": v(228, -6.28) * mm});
            skLineSegment(sketch, "E7.5.0.179", {"start": v(232, 1) * mm, "end": v(232, -1) * mm});
            skLineSegment(sketch, "E7.5.0.181", {"start": v(242, 9.55) * mm, "end": v(242, 4.27) * mm, "construction": true});
            skLineSegment(sketch, "E7.5.0.182", {"start": v(228, 1) * mm, "end": v(228, -1) * mm});
            skLineSegment(sketch, "E7.5.0.184", {"start": v(268, -4.28) * mm, "end": v(268, -6.28) * mm});
            skLineSegment(sketch, "E7.5.0.185", {"start": v(228, 1) * mm, "end": v(232, 1) * mm});
            skLineSegment(sketch, "E7.5.0.186", {"start": v(258, 1) * mm, "end": v(258, -1) * mm});
            skLineSegment(sketch, "E7.5.0.187", {"start": v(242, -4.28) * mm, "end": v(242, -6.28) * mm});
            skLineSegment(sketch, "E7.5.0.188", {"start": v(272, 9.55) * mm, "end": v(272, 4.27) * mm, "construction": true});
            skLineSegment(sketch, "E7.5.0.193", {"start": v(278, -1) * mm, "end": v(282, -1) * mm});
            skLineSegment(sketch, "E7.5.0.194", {"start": v(268, 4.27) * mm, "end": v(272, 4.27) * mm});
            skLineSegment(sketch, "E7.5.0.196", {"start": v(272, 6.27) * mm, "end": v(272, 4.27) * mm});
            skLineSegment(sketch, "E7.5.0.198", {"start": v(222, 11.55) * mm, "end": v(222, 9.55) * mm});
            skLineSegment(sketch, "E7.5.0.199", {"start": v(222, 1) * mm, "end": v(222, -1) * mm});
            skLineSegment(sketch, "E7.5.0.200", {"start": v(242, 6.27) * mm, "end": v(242, 4.27) * mm});
            skLineSegment(sketch, "E7.5.0.201", {"start": v(268, 6.27) * mm, "end": v(272, 6.27) * mm});
            skLineSegment(sketch, "E7.5.0.202", {"start": v(222, 9.55) * mm, "end": v(222, 4.27) * mm, "construction": true});
            skLineSegment(sketch, "E7.5.0.204", {"start": v(282, 1) * mm, "end": v(282, -1) * mm});
            skLineSegment(sketch, "E7.5.0.206", {"start": v(268, 6.27) * mm, "end": v(268, 4.27) * mm});
            skLineSegment(sketch, "E7.5.0.209", {"start": v(278, 1) * mm, "end": v(282, 1) * mm});
            skLineSegment(sketch, "E7.direction1", {"start": v(-272, -9.55) * mm, "end": v(-172, -9.55) * mm, "construction": true});
            skSolve(sketch);
        }
        {
            var Q0;
            Q0=qSketchRegion(id+"F2",true);
            extrude(context, id + "F3", {"entities" : qUnion([Q0]), "operationType" : NewBodyOperationType.ADD, "depth" : 1 * mm});
        }
        {
            var Q0;
            Q0=makeQuery(id+"F1.opExtrude","SWEPT_BODY",BODY,{"disambiguationData":[OSD([sQuery(id+"F0.wireOp",EDGE,"E0"),sQuery(id+"F0.wireOp",EDGE,"E1")])]});
            transform(context, id + "F4", {"entities" : qUnion([Q0]), "transformType" : TransformType.TRANSLATION_3D, "dx" : 0 * mm, "dy" : 0 * mm, "dz" : 0 * mm, "makeCopy" : true});
        }
        {
            var Q0;
            Q0=makeQuery(id+"F4.opPattern","COPY",FACE,{"derivedFrom":makeQuery(id+"F1.opExtrude","CAP_FACE",FACE,{"disambiguationData":[OSD([sQuery(id+"F0.wireOp",EDGE,"E0"),sQuery(id+"F0.wireOp",EDGE,"E1")])],"isStart":false}),"instanceName":"1"});
            var sketch = newSketch(context, id + "F5", { "sketchPlane" : qUnion([Q0])});
            skCircle(sketch, "E8", {"center": v(0, -6.27) * mm, "radius": 4 * mm});
            skSolve(sketch);
        }
        {
            var Q0;
            Q0=makeQuery(id+"F5.imprint","IMPRINT",FACE,{"disambiguationData":[TD([[makeQuery(id+"F5.imprint","IMPRINT",EDGE,{"derivedFrom":sQuery(id+"F5.wireOp",EDGE,"E8")}),1.0]])]});
            extrude(context, id + "F6", {"entities" : qUnion([Q0]), "operationType" : NewBodyOperationType.REMOVE, "endBound" : BoundingType.THROUGH_ALL, "oppositeDirection" : true, "depth" : 25 * mm});
        }
    });
